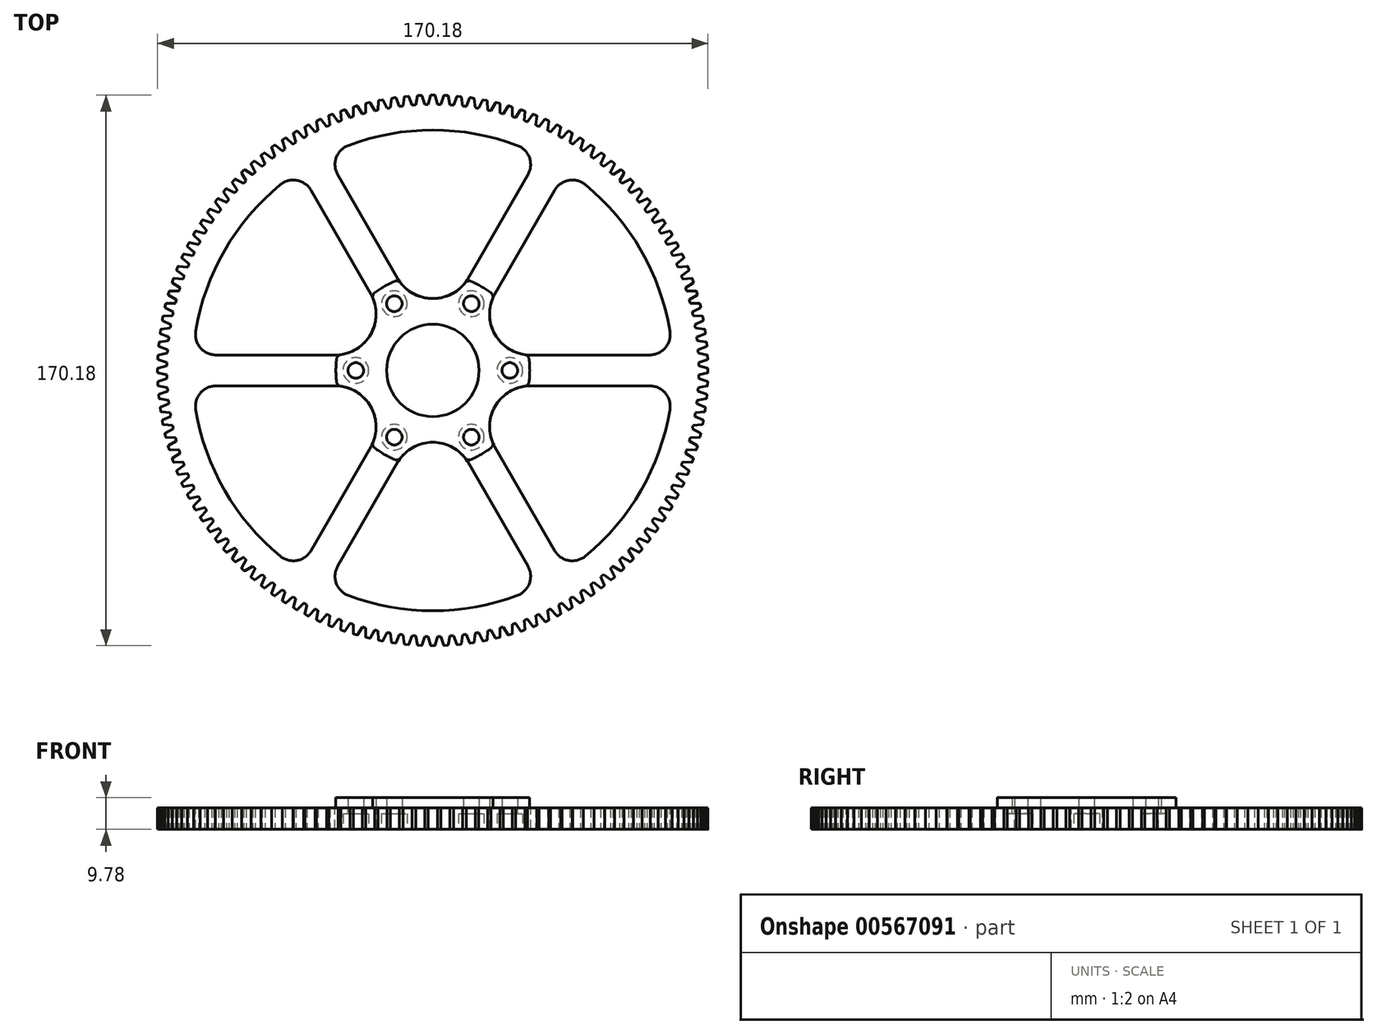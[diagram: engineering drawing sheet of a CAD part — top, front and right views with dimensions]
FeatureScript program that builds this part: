
annotation { "Feature Type Name" : "Feature", "Feature Type Description" : "" }
export const myFeature = defineFeature(function(context is Context, id is Id, definition is map)
    precondition{}
    {
        {
            var Q0;
            Q0=qCreatedBy(makeId("Top.planeOp"),FACE);
            var sketch = newSketch(context, id + "F0", { "sketchPlane" : qUnion([Q0])});
            skArc(sketch, "E0", {"start": v(-1.4, 82.23) * mm, "mid": v(-82.23, -1.4) * mm, "end": v(1.4, -82.23) * mm});
            skArc(sketch, "E1", {"start": v(1.4, -82.23) * mm, "mid": v(82.24, 0) * mm, "end": v(1.4, 82.23) * mm});
            skLineSegment(sketch, "E2", {"start": v(1.4, 82.23) * mm, "end": v(0.7, 84.97) * mm});
            skArc(sketch, "E3", {"start": v(0.7, 84.97) * mm, "mid": v(0.64, 85.06) * mm, "end": v(0.55, 85.1) * mm});
            skLineSegment(sketch, "E4", {"start": v(-1.4, 82.23) * mm, "end": v(-0.7, 84.97) * mm});
            skArc(sketch, "E5", {"start": v(-0.55, 85.1) * mm, "mid": v(-0.64, 85.06) * mm, "end": v(-0.7, 84.97) * mm});
            skLineSegment(sketch, "E6", {"start": v(-0.55, 85.1) * mm, "end": v(0.55, 85.1) * mm});
            skArc(sketch, "E7", {"start": v(1.4, 82.23) * mm, "mid": v(0, 82.24) * mm, "end": v(-1.4, 82.23) * mm});
            skSolve(sketch);
        }
        {
            var Q0;
            Q0=makeQuery(id+"F0.imprint","IMPRINT",FACE,{"disambiguationData":[TD([[makeQuery(id+"F0.imprint","IMPRINT",EDGE,{"derivedFrom":sQuery(id+"F0.wireOp",EDGE,"E0")}),1.0]])]});
            extrude(context, id + "F1", {"entities" : qUnion([Q0]), "endBound" : BoundingType.SYMMETRIC, "depth" : 6.6 * mm, "offsetDistance" : 25.4 * mm});
        }
        {
            var Q0;
            Q0=makeQuery(id+"F0.imprint","IMPRINT",FACE,{"disambiguationData":[TD([[makeQuery(id+"F0.imprint","IMPRINT",EDGE,{"derivedFrom":sQuery(id+"F0.wireOp",EDGE,"E2")}),1.0]])]});
            var Q1;
            Q1=makeQuery(id+"F1.opExtrude","CAP_FACE",FACE,{"disambiguationData":[OSD([sQuery(id+"F0.wireOp",EDGE,"E0"),sQuery(id+"F0.wireOp",EDGE,"E1"),sQuery(id+"F0.wireOp",EDGE,"E7")])],"isStart":false});
            var Q2;
            Q2=makeQuery(id+"F1.opExtrude","CAP_FACE",FACE,{"disambiguationData":[OSD([sQuery(id+"F0.wireOp",EDGE,"E0"),sQuery(id+"F0.wireOp",EDGE,"E1"),sQuery(id+"F0.wireOp",EDGE,"E7")])],"isStart":true});
            extrude(context, id + "F2", {"entities" : qUnion([Q0]), "endBound" : BoundingType.UP_TO_SURFACE, "endBoundEntityFace" : qUnion([Q1]), "depth" : 25.4 * mm, "hasSecondDirection" : true, "secondDirectionBound" : SecondDirectionBoundingType.UP_TO_SURFACE, "secondDirectionOppositeDirection" : true, "secondDirectionBoundEntityFace" : qUnion([Q2]), "secondDirectionDepth" : 25.4 * mm});
        }
        {
            var Q0;
            Q0=makeQuery(id+"F2.opExtrude","SWEPT_BODY",BODY,{"disambiguationData":[OSD([sQuery(id+"F0.wireOp",EDGE,"E2"),sQuery(id+"F0.wireOp",EDGE,"E3"),sQuery(id+"F0.wireOp",EDGE,"E4"),sQuery(id+"F0.wireOp",EDGE,"E5"),sQuery(id+"F0.wireOp",EDGE,"E6"),sQuery(id+"F0.wireOp",EDGE,"E7")])]});
            var Q1;
            Q1=makeQuery(id+"F1.opExtrude","CAP_EDGE",EDGE,{"disambiguationData":[OSD([sQuery(id+"F0.wireOp",EDGE,"E0"),sQuery(id+"F0.wireOp",EDGE,"E1"),sQuery(id+"F0.wireOp",EDGE,"E7")])],"isStart":false});
            circularPattern(context, id + "F3", {"operationType" : NewBodyOperationType.ADD, "entities" : qUnion([Q0]), "axis" : qUnion([Q1]), "angle" : 360 * degree, "instanceCount" : 132, "oppositeDirection" : true, "equalSpace" : true});
        }
        {
            var Q0;
            {var subQ0=sQuery(id+"F0.wireOp",EDGE,"E7");var subQ1=makeQuery(id+"F2.opExtrude","CAP_FACE",FACE,{"disambiguationData":[OSD([sQuery(id+"F0.wireOp",EDGE,"E2"),sQuery(id+"F0.wireOp",EDGE,"E3"),sQuery(id+"F0.wireOp",EDGE,"E4"),sQuery(id+"F0.wireOp",EDGE,"E5"),sQuery(id+"F0.wireOp",EDGE,"E6"),subQ0])],"isStart":false});Q0=makeQuery(id+"F3.boolean.opBoolean","MERGE",FACE,{"derivedFrom":[makeQuery(id+"F1.opExtrude","CAP_FACE",FACE,{"disambiguationData":[OSD([sQuery(id+"F0.wireOp",EDGE,"E0"),sQuery(id+"F0.wireOp",EDGE,"E1"),subQ0])],"isStart":false}),subQ1,makeQuery(id+"F3.opPattern","COPY",FACE,{"derivedFrom":subQ1,"instanceName":"1"}),makeQuery(id+"F3.opPattern","COPY",FACE,{"derivedFrom":subQ1,"instanceName":"2"}),makeQuery(id+"F3.opPattern","COPY",FACE,{"derivedFrom":subQ1,"instanceName":"3"}),makeQuery(id+"F3.opPattern","COPY",FACE,{"derivedFrom":subQ1,"instanceName":"4"}),makeQuery(id+"F3.opPattern","COPY",FACE,{"derivedFrom":subQ1,"instanceName":"5"}),makeQuery(id+"F3.opPattern","COPY",FACE,{"derivedFrom":subQ1,"instanceName":"6"}),makeQuery(id+"F3.opPattern","COPY",FACE,{"derivedFrom":subQ1,"instanceName":"7"}),makeQuery(id+"F3.opPattern","COPY",FACE,{"derivedFrom":subQ1,"instanceName":"8"}),makeQuery(id+"F3.opPattern","COPY",FACE,{"derivedFrom":subQ1,"instanceName":"9"}),makeQuery(id+"F3.opPattern","COPY",FACE,{"derivedFrom":subQ1,"instanceName":"10"}),makeQuery(id+"F3.opPattern","COPY",FACE,{"derivedFrom":subQ1,"instanceName":"11"}),makeQuery(id+"F3.opPattern","COPY",FACE,{"derivedFrom":subQ1,"instanceName":"12"}),makeQuery(id+"F3.opPattern","COPY",FACE,{"derivedFrom":subQ1,"instanceName":"13"}),makeQuery(id+"F3.opPattern","COPY",FACE,{"derivedFrom":subQ1,"instanceName":"14"}),makeQuery(id+"F3.opPattern","COPY",FACE,{"derivedFrom":subQ1,"instanceName":"15"}),makeQuery(id+"F3.opPattern","COPY",FACE,{"derivedFrom":subQ1,"instanceName":"16"}),makeQuery(id+"F3.opPattern","COPY",FACE,{"derivedFrom":subQ1,"instanceName":"17"}),makeQuery(id+"F3.opPattern","COPY",FACE,{"derivedFrom":subQ1,"instanceName":"18"}),makeQuery(id+"F3.opPattern","COPY",FACE,{"derivedFrom":subQ1,"instanceName":"19"}),makeQuery(id+"F3.opPattern","COPY",FACE,{"derivedFrom":subQ1,"instanceName":"20"}),makeQuery(id+"F3.opPattern","COPY",FACE,{"derivedFrom":subQ1,"instanceName":"21"}),makeQuery(id+"F3.opPattern","COPY",FACE,{"derivedFrom":subQ1,"instanceName":"22"}),makeQuery(id+"F3.opPattern","COPY",FACE,{"derivedFrom":subQ1,"instanceName":"23"}),makeQuery(id+"F3.opPattern","COPY",FACE,{"derivedFrom":subQ1,"instanceName":"24"}),makeQuery(id+"F3.opPattern","COPY",FACE,{"derivedFrom":subQ1,"instanceName":"25"}),makeQuery(id+"F3.opPattern","COPY",FACE,{"derivedFrom":subQ1,"instanceName":"26"}),makeQuery(id+"F3.opPattern","COPY",FACE,{"derivedFrom":subQ1,"instanceName":"27"}),makeQuery(id+"F3.opPattern","COPY",FACE,{"derivedFrom":subQ1,"instanceName":"28"}),makeQuery(id+"F3.opPattern","COPY",FACE,{"derivedFrom":subQ1,"instanceName":"29"}),makeQuery(id+"F3.opPattern","COPY",FACE,{"derivedFrom":subQ1,"instanceName":"30"}),makeQuery(id+"F3.opPattern","COPY",FACE,{"derivedFrom":subQ1,"instanceName":"31"}),makeQuery(id+"F3.opPattern","COPY",FACE,{"derivedFrom":subQ1,"instanceName":"32"}),makeQuery(id+"F3.opPattern","COPY",FACE,{"derivedFrom":subQ1,"instanceName":"33"}),makeQuery(id+"F3.opPattern","COPY",FACE,{"derivedFrom":subQ1,"instanceName":"34"}),makeQuery(id+"F3.opPattern","COPY",FACE,{"derivedFrom":subQ1,"instanceName":"35"}),makeQuery(id+"F3.opPattern","COPY",FACE,{"derivedFrom":subQ1,"instanceName":"36"}),makeQuery(id+"F3.opPattern","COPY",FACE,{"derivedFrom":subQ1,"instanceName":"37"}),makeQuery(id+"F3.opPattern","COPY",FACE,{"derivedFrom":subQ1,"instanceName":"38"}),makeQuery(id+"F3.opPattern","COPY",FACE,{"derivedFrom":subQ1,"instanceName":"39"}),makeQuery(id+"F3.opPattern","COPY",FACE,{"derivedFrom":subQ1,"instanceName":"40"}),makeQuery(id+"F3.opPattern","COPY",FACE,{"derivedFrom":subQ1,"instanceName":"41"}),makeQuery(id+"F3.opPattern","COPY",FACE,{"derivedFrom":subQ1,"instanceName":"42"}),makeQuery(id+"F3.opPattern","COPY",FACE,{"derivedFrom":subQ1,"instanceName":"43"}),makeQuery(id+"F3.opPattern","COPY",FACE,{"derivedFrom":subQ1,"instanceName":"44"}),makeQuery(id+"F3.opPattern","COPY",FACE,{"derivedFrom":subQ1,"instanceName":"45"}),makeQuery(id+"F3.opPattern","COPY",FACE,{"derivedFrom":subQ1,"instanceName":"46"}),makeQuery(id+"F3.opPattern","COPY",FACE,{"derivedFrom":subQ1,"instanceName":"47"}),makeQuery(id+"F3.opPattern","COPY",FACE,{"derivedFrom":subQ1,"instanceName":"48"}),makeQuery(id+"F3.opPattern","COPY",FACE,{"derivedFrom":subQ1,"instanceName":"49"}),makeQuery(id+"F3.opPattern","COPY",FACE,{"derivedFrom":subQ1,"instanceName":"50"}),makeQuery(id+"F3.opPattern","COPY",FACE,{"derivedFrom":subQ1,"instanceName":"51"}),makeQuery(id+"F3.opPattern","COPY",FACE,{"derivedFrom":subQ1,"instanceName":"52"}),makeQuery(id+"F3.opPattern","COPY",FACE,{"derivedFrom":subQ1,"instanceName":"53"}),makeQuery(id+"F3.opPattern","COPY",FACE,{"derivedFrom":subQ1,"instanceName":"54"}),makeQuery(id+"F3.opPattern","COPY",FACE,{"derivedFrom":subQ1,"instanceName":"55"}),makeQuery(id+"F3.opPattern","COPY",FACE,{"derivedFrom":subQ1,"instanceName":"56"}),makeQuery(id+"F3.opPattern","COPY",FACE,{"derivedFrom":subQ1,"instanceName":"57"}),makeQuery(id+"F3.opPattern","COPY",FACE,{"derivedFrom":subQ1,"instanceName":"58"}),makeQuery(id+"F3.opPattern","COPY",FACE,{"derivedFrom":subQ1,"instanceName":"59"}),makeQuery(id+"F3.opPattern","COPY",FACE,{"derivedFrom":subQ1,"instanceName":"60"}),makeQuery(id+"F3.opPattern","COPY",FACE,{"derivedFrom":subQ1,"instanceName":"61"}),makeQuery(id+"F3.opPattern","COPY",FACE,{"derivedFrom":subQ1,"instanceName":"62"}),makeQuery(id+"F3.opPattern","COPY",FACE,{"derivedFrom":subQ1,"instanceName":"63"}),makeQuery(id+"F3.opPattern","COPY",FACE,{"derivedFrom":subQ1,"instanceName":"64"}),makeQuery(id+"F3.opPattern","COPY",FACE,{"derivedFrom":subQ1,"instanceName":"65"}),makeQuery(id+"F3.opPattern","COPY",FACE,{"derivedFrom":subQ1,"instanceName":"66"}),makeQuery(id+"F3.opPattern","COPY",FACE,{"derivedFrom":subQ1,"instanceName":"67"}),makeQuery(id+"F3.opPattern","COPY",FACE,{"derivedFrom":subQ1,"instanceName":"68"}),makeQuery(id+"F3.opPattern","COPY",FACE,{"derivedFrom":subQ1,"instanceName":"69"}),makeQuery(id+"F3.opPattern","COPY",FACE,{"derivedFrom":subQ1,"instanceName":"70"}),makeQuery(id+"F3.opPattern","COPY",FACE,{"derivedFrom":subQ1,"instanceName":"71"}),makeQuery(id+"F3.opPattern","COPY",FACE,{"derivedFrom":subQ1,"instanceName":"72"}),makeQuery(id+"F3.opPattern","COPY",FACE,{"derivedFrom":subQ1,"instanceName":"73"}),makeQuery(id+"F3.opPattern","COPY",FACE,{"derivedFrom":subQ1,"instanceName":"74"}),makeQuery(id+"F3.opPattern","COPY",FACE,{"derivedFrom":subQ1,"instanceName":"75"}),makeQuery(id+"F3.opPattern","COPY",FACE,{"derivedFrom":subQ1,"instanceName":"76"}),makeQuery(id+"F3.opPattern","COPY",FACE,{"derivedFrom":subQ1,"instanceName":"77"}),makeQuery(id+"F3.opPattern","COPY",FACE,{"derivedFrom":subQ1,"instanceName":"78"}),makeQuery(id+"F3.opPattern","COPY",FACE,{"derivedFrom":subQ1,"instanceName":"79"}),makeQuery(id+"F3.opPattern","COPY",FACE,{"derivedFrom":subQ1,"instanceName":"80"}),makeQuery(id+"F3.opPattern","COPY",FACE,{"derivedFrom":subQ1,"instanceName":"81"}),makeQuery(id+"F3.opPattern","COPY",FACE,{"derivedFrom":subQ1,"instanceName":"82"}),makeQuery(id+"F3.opPattern","COPY",FACE,{"derivedFrom":subQ1,"instanceName":"83"}),makeQuery(id+"F3.opPattern","COPY",FACE,{"derivedFrom":subQ1,"instanceName":"84"}),makeQuery(id+"F3.opPattern","COPY",FACE,{"derivedFrom":subQ1,"instanceName":"85"}),makeQuery(id+"F3.opPattern","COPY",FACE,{"derivedFrom":subQ1,"instanceName":"86"}),makeQuery(id+"F3.opPattern","COPY",FACE,{"derivedFrom":subQ1,"instanceName":"87"}),makeQuery(id+"F3.opPattern","COPY",FACE,{"derivedFrom":subQ1,"instanceName":"88"}),makeQuery(id+"F3.opPattern","COPY",FACE,{"derivedFrom":subQ1,"instanceName":"89"}),makeQuery(id+"F3.opPattern","COPY",FACE,{"derivedFrom":subQ1,"instanceName":"90"}),makeQuery(id+"F3.opPattern","COPY",FACE,{"derivedFrom":subQ1,"instanceName":"91"}),makeQuery(id+"F3.opPattern","COPY",FACE,{"derivedFrom":subQ1,"instanceName":"92"}),makeQuery(id+"F3.opPattern","COPY",FACE,{"derivedFrom":subQ1,"instanceName":"93"}),makeQuery(id+"F3.opPattern","COPY",FACE,{"derivedFrom":subQ1,"instanceName":"94"}),makeQuery(id+"F3.opPattern","COPY",FACE,{"derivedFrom":subQ1,"instanceName":"95"}),makeQuery(id+"F3.opPattern","COPY",FACE,{"derivedFrom":subQ1,"instanceName":"96"}),makeQuery(id+"F3.opPattern","COPY",FACE,{"derivedFrom":subQ1,"instanceName":"97"}),makeQuery(id+"F3.opPattern","COPY",FACE,{"derivedFrom":subQ1,"instanceName":"98"}),makeQuery(id+"F3.opPattern","COPY",FACE,{"derivedFrom":subQ1,"instanceName":"99"}),makeQuery(id+"F3.opPattern","COPY",FACE,{"derivedFrom":subQ1,"instanceName":"100"}),makeQuery(id+"F3.opPattern","COPY",FACE,{"derivedFrom":subQ1,"instanceName":"101"}),makeQuery(id+"F3.opPattern","COPY",FACE,{"derivedFrom":subQ1,"instanceName":"102"}),makeQuery(id+"F3.opPattern","COPY",FACE,{"derivedFrom":subQ1,"instanceName":"103"}),makeQuery(id+"F3.opPattern","COPY",FACE,{"derivedFrom":subQ1,"instanceName":"104"}),makeQuery(id+"F3.opPattern","COPY",FACE,{"derivedFrom":subQ1,"instanceName":"105"}),makeQuery(id+"F3.opPattern","COPY",FACE,{"derivedFrom":subQ1,"instanceName":"106"}),makeQuery(id+"F3.opPattern","COPY",FACE,{"derivedFrom":subQ1,"instanceName":"107"}),makeQuery(id+"F3.opPattern","COPY",FACE,{"derivedFrom":subQ1,"instanceName":"108"}),makeQuery(id+"F3.opPattern","COPY",FACE,{"derivedFrom":subQ1,"instanceName":"109"}),makeQuery(id+"F3.opPattern","COPY",FACE,{"derivedFrom":subQ1,"instanceName":"110"}),makeQuery(id+"F3.opPattern","COPY",FACE,{"derivedFrom":subQ1,"instanceName":"111"}),makeQuery(id+"F3.opPattern","COPY",FACE,{"derivedFrom":subQ1,"instanceName":"112"}),makeQuery(id+"F3.opPattern","COPY",FACE,{"derivedFrom":subQ1,"instanceName":"113"}),makeQuery(id+"F3.opPattern","COPY",FACE,{"derivedFrom":subQ1,"instanceName":"114"}),makeQuery(id+"F3.opPattern","COPY",FACE,{"derivedFrom":subQ1,"instanceName":"115"}),makeQuery(id+"F3.opPattern","COPY",FACE,{"derivedFrom":subQ1,"instanceName":"116"}),makeQuery(id+"F3.opPattern","COPY",FACE,{"derivedFrom":subQ1,"instanceName":"117"}),makeQuery(id+"F3.opPattern","COPY",FACE,{"derivedFrom":subQ1,"instanceName":"118"}),makeQuery(id+"F3.opPattern","COPY",FACE,{"derivedFrom":subQ1,"instanceName":"119"}),makeQuery(id+"F3.opPattern","COPY",FACE,{"derivedFrom":subQ1,"instanceName":"120"}),makeQuery(id+"F3.opPattern","COPY",FACE,{"derivedFrom":subQ1,"instanceName":"121"}),makeQuery(id+"F3.opPattern","COPY",FACE,{"derivedFrom":subQ1,"instanceName":"122"}),makeQuery(id+"F3.opPattern","COPY",FACE,{"derivedFrom":subQ1,"instanceName":"123"}),makeQuery(id+"F3.opPattern","COPY",FACE,{"derivedFrom":subQ1,"instanceName":"124"}),makeQuery(id+"F3.opPattern","COPY",FACE,{"derivedFrom":subQ1,"instanceName":"125"}),makeQuery(id+"F3.opPattern","COPY",FACE,{"derivedFrom":subQ1,"instanceName":"126"}),makeQuery(id+"F3.opPattern","COPY",FACE,{"derivedFrom":subQ1,"instanceName":"127"}),makeQuery(id+"F3.opPattern","COPY",FACE,{"derivedFrom":subQ1,"instanceName":"128"}),makeQuery(id+"F3.opPattern","COPY",FACE,{"derivedFrom":subQ1,"instanceName":"129"}),makeQuery(id+"F3.opPattern","COPY",FACE,{"derivedFrom":subQ1,"instanceName":"130"}),makeQuery(id+"F3.opPattern","COPY",FACE,{"derivedFrom":subQ1,"instanceName":"131"})]});}
            var sketch = newSketch(context, id + "F4", { "sketchPlane" : qUnion([Q0])});
            skCircle(sketch, "E8", {"center": v(0, 0) * mm, "radius": 14.29 * mm});
            skCircle(sketch, "E9.cCircle", {"center": v(0, 0) * mm, "radius": 23.81 * mm, "construction": true});
            skLineSegment(sketch, "E9.0", {"start": v(23.81, 0) * mm, "end": v(11.9, -20.62) * mm, "construction": true});
            skLineSegment(sketch, "E9.1", {"start": v(11.9, -20.62) * mm, "end": v(-11.9, -20.62) * mm, "construction": true});
            skLineSegment(sketch, "E9.2", {"start": v(-11.9, -20.62) * mm, "end": v(-23.81, 0) * mm, "construction": true});
            skLineSegment(sketch, "E9.3", {"start": v(-23.81, 0) * mm, "end": v(-11.9, 20.62) * mm, "construction": true});
            skLineSegment(sketch, "E9.4", {"start": v(-11.9, 20.62) * mm, "end": v(11.9, 20.62) * mm, "construction": true});
            skLineSegment(sketch, "E9.5", {"start": v(11.9, 20.62) * mm, "end": v(23.81, 0) * mm, "construction": true});
            skCircle(sketch, "E10", {"center": v(-11.9, 20.62) * mm, "radius": 2.41 * mm});
            skCircle(sketch, "E11", {"center": v(-23.81, 0) * mm, "radius": 2.41 * mm});
            skCircle(sketch, "E12", {"center": v(-11.9, -20.62) * mm, "radius": 2.41 * mm});
            skCircle(sketch, "E13", {"center": v(11.9, -20.62) * mm, "radius": 2.41 * mm});
            skCircle(sketch, "E14", {"center": v(23.81, 0) * mm, "radius": 2.41 * mm});
            skCircle(sketch, "E15", {"center": v(11.9, 20.62) * mm, "radius": 2.41 * mm});
            skSolve(sketch);
        }
        {
            var Q0;
            Q0=qSketchRegion(id+"F4",true);
            extrude(context, id + "F5", {"entities" : qUnion([Q0]), "operationType" : NewBodyOperationType.REMOVE, "endBound" : BoundingType.THROUGH_ALL, "oppositeDirection" : true, "depth" : 25.4 * mm});
        }
        {
            var Q0;
            {var subQ0=sQuery(id+"F0.wireOp",EDGE,"E7");var subQ1=makeQuery(id+"F2.opExtrude","CAP_FACE",FACE,{"disambiguationData":[OSD([sQuery(id+"F0.wireOp",EDGE,"E2"),sQuery(id+"F0.wireOp",EDGE,"E3"),sQuery(id+"F0.wireOp",EDGE,"E4"),sQuery(id+"F0.wireOp",EDGE,"E5"),sQuery(id+"F0.wireOp",EDGE,"E6"),subQ0])],"isStart":false});Q0=makeQuery(id+"F3.boolean.opBoolean","MERGE",FACE,{"derivedFrom":[makeQuery(id+"F1.opExtrude","CAP_FACE",FACE,{"disambiguationData":[OSD([sQuery(id+"F0.wireOp",EDGE,"E0"),sQuery(id+"F0.wireOp",EDGE,"E1"),subQ0])],"isStart":false}),subQ1,makeQuery(id+"F3.opPattern","COPY",FACE,{"derivedFrom":subQ1,"instanceName":"1"}),makeQuery(id+"F3.opPattern","COPY",FACE,{"derivedFrom":subQ1,"instanceName":"2"}),makeQuery(id+"F3.opPattern","COPY",FACE,{"derivedFrom":subQ1,"instanceName":"3"}),makeQuery(id+"F3.opPattern","COPY",FACE,{"derivedFrom":subQ1,"instanceName":"4"}),makeQuery(id+"F3.opPattern","COPY",FACE,{"derivedFrom":subQ1,"instanceName":"5"}),makeQuery(id+"F3.opPattern","COPY",FACE,{"derivedFrom":subQ1,"instanceName":"6"}),makeQuery(id+"F3.opPattern","COPY",FACE,{"derivedFrom":subQ1,"instanceName":"7"}),makeQuery(id+"F3.opPattern","COPY",FACE,{"derivedFrom":subQ1,"instanceName":"8"}),makeQuery(id+"F3.opPattern","COPY",FACE,{"derivedFrom":subQ1,"instanceName":"9"}),makeQuery(id+"F3.opPattern","COPY",FACE,{"derivedFrom":subQ1,"instanceName":"10"}),makeQuery(id+"F3.opPattern","COPY",FACE,{"derivedFrom":subQ1,"instanceName":"11"}),makeQuery(id+"F3.opPattern","COPY",FACE,{"derivedFrom":subQ1,"instanceName":"12"}),makeQuery(id+"F3.opPattern","COPY",FACE,{"derivedFrom":subQ1,"instanceName":"13"}),makeQuery(id+"F3.opPattern","COPY",FACE,{"derivedFrom":subQ1,"instanceName":"14"}),makeQuery(id+"F3.opPattern","COPY",FACE,{"derivedFrom":subQ1,"instanceName":"15"}),makeQuery(id+"F3.opPattern","COPY",FACE,{"derivedFrom":subQ1,"instanceName":"16"}),makeQuery(id+"F3.opPattern","COPY",FACE,{"derivedFrom":subQ1,"instanceName":"17"}),makeQuery(id+"F3.opPattern","COPY",FACE,{"derivedFrom":subQ1,"instanceName":"18"}),makeQuery(id+"F3.opPattern","COPY",FACE,{"derivedFrom":subQ1,"instanceName":"19"}),makeQuery(id+"F3.opPattern","COPY",FACE,{"derivedFrom":subQ1,"instanceName":"20"}),makeQuery(id+"F3.opPattern","COPY",FACE,{"derivedFrom":subQ1,"instanceName":"21"}),makeQuery(id+"F3.opPattern","COPY",FACE,{"derivedFrom":subQ1,"instanceName":"22"}),makeQuery(id+"F3.opPattern","COPY",FACE,{"derivedFrom":subQ1,"instanceName":"23"}),makeQuery(id+"F3.opPattern","COPY",FACE,{"derivedFrom":subQ1,"instanceName":"24"}),makeQuery(id+"F3.opPattern","COPY",FACE,{"derivedFrom":subQ1,"instanceName":"25"}),makeQuery(id+"F3.opPattern","COPY",FACE,{"derivedFrom":subQ1,"instanceName":"26"}),makeQuery(id+"F3.opPattern","COPY",FACE,{"derivedFrom":subQ1,"instanceName":"27"}),makeQuery(id+"F3.opPattern","COPY",FACE,{"derivedFrom":subQ1,"instanceName":"28"}),makeQuery(id+"F3.opPattern","COPY",FACE,{"derivedFrom":subQ1,"instanceName":"29"}),makeQuery(id+"F3.opPattern","COPY",FACE,{"derivedFrom":subQ1,"instanceName":"30"}),makeQuery(id+"F3.opPattern","COPY",FACE,{"derivedFrom":subQ1,"instanceName":"31"}),makeQuery(id+"F3.opPattern","COPY",FACE,{"derivedFrom":subQ1,"instanceName":"32"}),makeQuery(id+"F3.opPattern","COPY",FACE,{"derivedFrom":subQ1,"instanceName":"33"}),makeQuery(id+"F3.opPattern","COPY",FACE,{"derivedFrom":subQ1,"instanceName":"34"}),makeQuery(id+"F3.opPattern","COPY",FACE,{"derivedFrom":subQ1,"instanceName":"35"}),makeQuery(id+"F3.opPattern","COPY",FACE,{"derivedFrom":subQ1,"instanceName":"36"}),makeQuery(id+"F3.opPattern","COPY",FACE,{"derivedFrom":subQ1,"instanceName":"37"}),makeQuery(id+"F3.opPattern","COPY",FACE,{"derivedFrom":subQ1,"instanceName":"38"}),makeQuery(id+"F3.opPattern","COPY",FACE,{"derivedFrom":subQ1,"instanceName":"39"}),makeQuery(id+"F3.opPattern","COPY",FACE,{"derivedFrom":subQ1,"instanceName":"40"}),makeQuery(id+"F3.opPattern","COPY",FACE,{"derivedFrom":subQ1,"instanceName":"41"}),makeQuery(id+"F3.opPattern","COPY",FACE,{"derivedFrom":subQ1,"instanceName":"42"}),makeQuery(id+"F3.opPattern","COPY",FACE,{"derivedFrom":subQ1,"instanceName":"43"}),makeQuery(id+"F3.opPattern","COPY",FACE,{"derivedFrom":subQ1,"instanceName":"44"}),makeQuery(id+"F3.opPattern","COPY",FACE,{"derivedFrom":subQ1,"instanceName":"45"}),makeQuery(id+"F3.opPattern","COPY",FACE,{"derivedFrom":subQ1,"instanceName":"46"}),makeQuery(id+"F3.opPattern","COPY",FACE,{"derivedFrom":subQ1,"instanceName":"47"}),makeQuery(id+"F3.opPattern","COPY",FACE,{"derivedFrom":subQ1,"instanceName":"48"}),makeQuery(id+"F3.opPattern","COPY",FACE,{"derivedFrom":subQ1,"instanceName":"49"}),makeQuery(id+"F3.opPattern","COPY",FACE,{"derivedFrom":subQ1,"instanceName":"50"}),makeQuery(id+"F3.opPattern","COPY",FACE,{"derivedFrom":subQ1,"instanceName":"51"}),makeQuery(id+"F3.opPattern","COPY",FACE,{"derivedFrom":subQ1,"instanceName":"52"}),makeQuery(id+"F3.opPattern","COPY",FACE,{"derivedFrom":subQ1,"instanceName":"53"}),makeQuery(id+"F3.opPattern","COPY",FACE,{"derivedFrom":subQ1,"instanceName":"54"}),makeQuery(id+"F3.opPattern","COPY",FACE,{"derivedFrom":subQ1,"instanceName":"55"}),makeQuery(id+"F3.opPattern","COPY",FACE,{"derivedFrom":subQ1,"instanceName":"56"}),makeQuery(id+"F3.opPattern","COPY",FACE,{"derivedFrom":subQ1,"instanceName":"57"}),makeQuery(id+"F3.opPattern","COPY",FACE,{"derivedFrom":subQ1,"instanceName":"58"}),makeQuery(id+"F3.opPattern","COPY",FACE,{"derivedFrom":subQ1,"instanceName":"59"}),makeQuery(id+"F3.opPattern","COPY",FACE,{"derivedFrom":subQ1,"instanceName":"60"}),makeQuery(id+"F3.opPattern","COPY",FACE,{"derivedFrom":subQ1,"instanceName":"61"}),makeQuery(id+"F3.opPattern","COPY",FACE,{"derivedFrom":subQ1,"instanceName":"62"}),makeQuery(id+"F3.opPattern","COPY",FACE,{"derivedFrom":subQ1,"instanceName":"63"}),makeQuery(id+"F3.opPattern","COPY",FACE,{"derivedFrom":subQ1,"instanceName":"64"}),makeQuery(id+"F3.opPattern","COPY",FACE,{"derivedFrom":subQ1,"instanceName":"65"}),makeQuery(id+"F3.opPattern","COPY",FACE,{"derivedFrom":subQ1,"instanceName":"66"}),makeQuery(id+"F3.opPattern","COPY",FACE,{"derivedFrom":subQ1,"instanceName":"67"}),makeQuery(id+"F3.opPattern","COPY",FACE,{"derivedFrom":subQ1,"instanceName":"68"}),makeQuery(id+"F3.opPattern","COPY",FACE,{"derivedFrom":subQ1,"instanceName":"69"}),makeQuery(id+"F3.opPattern","COPY",FACE,{"derivedFrom":subQ1,"instanceName":"70"}),makeQuery(id+"F3.opPattern","COPY",FACE,{"derivedFrom":subQ1,"instanceName":"71"}),makeQuery(id+"F3.opPattern","COPY",FACE,{"derivedFrom":subQ1,"instanceName":"72"}),makeQuery(id+"F3.opPattern","COPY",FACE,{"derivedFrom":subQ1,"instanceName":"73"}),makeQuery(id+"F3.opPattern","COPY",FACE,{"derivedFrom":subQ1,"instanceName":"74"}),makeQuery(id+"F3.opPattern","COPY",FACE,{"derivedFrom":subQ1,"instanceName":"75"}),makeQuery(id+"F3.opPattern","COPY",FACE,{"derivedFrom":subQ1,"instanceName":"76"}),makeQuery(id+"F3.opPattern","COPY",FACE,{"derivedFrom":subQ1,"instanceName":"77"}),makeQuery(id+"F3.opPattern","COPY",FACE,{"derivedFrom":subQ1,"instanceName":"78"}),makeQuery(id+"F3.opPattern","COPY",FACE,{"derivedFrom":subQ1,"instanceName":"79"}),makeQuery(id+"F3.opPattern","COPY",FACE,{"derivedFrom":subQ1,"instanceName":"80"}),makeQuery(id+"F3.opPattern","COPY",FACE,{"derivedFrom":subQ1,"instanceName":"81"}),makeQuery(id+"F3.opPattern","COPY",FACE,{"derivedFrom":subQ1,"instanceName":"82"}),makeQuery(id+"F3.opPattern","COPY",FACE,{"derivedFrom":subQ1,"instanceName":"83"}),makeQuery(id+"F3.opPattern","COPY",FACE,{"derivedFrom":subQ1,"instanceName":"84"}),makeQuery(id+"F3.opPattern","COPY",FACE,{"derivedFrom":subQ1,"instanceName":"85"}),makeQuery(id+"F3.opPattern","COPY",FACE,{"derivedFrom":subQ1,"instanceName":"86"}),makeQuery(id+"F3.opPattern","COPY",FACE,{"derivedFrom":subQ1,"instanceName":"87"}),makeQuery(id+"F3.opPattern","COPY",FACE,{"derivedFrom":subQ1,"instanceName":"88"}),makeQuery(id+"F3.opPattern","COPY",FACE,{"derivedFrom":subQ1,"instanceName":"89"}),makeQuery(id+"F3.opPattern","COPY",FACE,{"derivedFrom":subQ1,"instanceName":"90"}),makeQuery(id+"F3.opPattern","COPY",FACE,{"derivedFrom":subQ1,"instanceName":"91"}),makeQuery(id+"F3.opPattern","COPY",FACE,{"derivedFrom":subQ1,"instanceName":"92"}),makeQuery(id+"F3.opPattern","COPY",FACE,{"derivedFrom":subQ1,"instanceName":"93"}),makeQuery(id+"F3.opPattern","COPY",FACE,{"derivedFrom":subQ1,"instanceName":"94"}),makeQuery(id+"F3.opPattern","COPY",FACE,{"derivedFrom":subQ1,"instanceName":"95"}),makeQuery(id+"F3.opPattern","COPY",FACE,{"derivedFrom":subQ1,"instanceName":"96"}),makeQuery(id+"F3.opPattern","COPY",FACE,{"derivedFrom":subQ1,"instanceName":"97"}),makeQuery(id+"F3.opPattern","COPY",FACE,{"derivedFrom":subQ1,"instanceName":"98"}),makeQuery(id+"F3.opPattern","COPY",FACE,{"derivedFrom":subQ1,"instanceName":"99"}),makeQuery(id+"F3.opPattern","COPY",FACE,{"derivedFrom":subQ1,"instanceName":"100"}),makeQuery(id+"F3.opPattern","COPY",FACE,{"derivedFrom":subQ1,"instanceName":"101"}),makeQuery(id+"F3.opPattern","COPY",FACE,{"derivedFrom":subQ1,"instanceName":"102"}),makeQuery(id+"F3.opPattern","COPY",FACE,{"derivedFrom":subQ1,"instanceName":"103"}),makeQuery(id+"F3.opPattern","COPY",FACE,{"derivedFrom":subQ1,"instanceName":"104"}),makeQuery(id+"F3.opPattern","COPY",FACE,{"derivedFrom":subQ1,"instanceName":"105"}),makeQuery(id+"F3.opPattern","COPY",FACE,{"derivedFrom":subQ1,"instanceName":"106"}),makeQuery(id+"F3.opPattern","COPY",FACE,{"derivedFrom":subQ1,"instanceName":"107"}),makeQuery(id+"F3.opPattern","COPY",FACE,{"derivedFrom":subQ1,"instanceName":"108"}),makeQuery(id+"F3.opPattern","COPY",FACE,{"derivedFrom":subQ1,"instanceName":"109"}),makeQuery(id+"F3.opPattern","COPY",FACE,{"derivedFrom":subQ1,"instanceName":"110"}),makeQuery(id+"F3.opPattern","COPY",FACE,{"derivedFrom":subQ1,"instanceName":"111"}),makeQuery(id+"F3.opPattern","COPY",FACE,{"derivedFrom":subQ1,"instanceName":"112"}),makeQuery(id+"F3.opPattern","COPY",FACE,{"derivedFrom":subQ1,"instanceName":"113"}),makeQuery(id+"F3.opPattern","COPY",FACE,{"derivedFrom":subQ1,"instanceName":"114"}),makeQuery(id+"F3.opPattern","COPY",FACE,{"derivedFrom":subQ1,"instanceName":"115"}),makeQuery(id+"F3.opPattern","COPY",FACE,{"derivedFrom":subQ1,"instanceName":"116"}),makeQuery(id+"F3.opPattern","COPY",FACE,{"derivedFrom":subQ1,"instanceName":"117"}),makeQuery(id+"F3.opPattern","COPY",FACE,{"derivedFrom":subQ1,"instanceName":"118"}),makeQuery(id+"F3.opPattern","COPY",FACE,{"derivedFrom":subQ1,"instanceName":"119"}),makeQuery(id+"F3.opPattern","COPY",FACE,{"derivedFrom":subQ1,"instanceName":"120"}),makeQuery(id+"F3.opPattern","COPY",FACE,{"derivedFrom":subQ1,"instanceName":"121"}),makeQuery(id+"F3.opPattern","COPY",FACE,{"derivedFrom":subQ1,"instanceName":"122"}),makeQuery(id+"F3.opPattern","COPY",FACE,{"derivedFrom":subQ1,"instanceName":"123"}),makeQuery(id+"F3.opPattern","COPY",FACE,{"derivedFrom":subQ1,"instanceName":"124"}),makeQuery(id+"F3.opPattern","COPY",FACE,{"derivedFrom":subQ1,"instanceName":"125"}),makeQuery(id+"F3.opPattern","COPY",FACE,{"derivedFrom":subQ1,"instanceName":"126"}),makeQuery(id+"F3.opPattern","COPY",FACE,{"derivedFrom":subQ1,"instanceName":"127"}),makeQuery(id+"F3.opPattern","COPY",FACE,{"derivedFrom":subQ1,"instanceName":"128"}),makeQuery(id+"F3.opPattern","COPY",FACE,{"derivedFrom":subQ1,"instanceName":"129"}),makeQuery(id+"F3.opPattern","COPY",FACE,{"derivedFrom":subQ1,"instanceName":"130"}),makeQuery(id+"F3.opPattern","COPY",FACE,{"derivedFrom":subQ1,"instanceName":"131"})]});}
            var sketch = newSketch(context, id + "F6", { "sketchPlane" : qUnion([Q0])});
            skArc(sketch, "E16", {"start": v(-37.15, 64.35) * mm, "mid": v(-64.35, 37.15) * mm, "end": v(-74.3, 0) * mm});
            skArc(sketch, "E17", {"start": v(-15.08, 26.12) * mm, "mid": v(-26.12, 15.08) * mm, "end": v(-30.16, 0) * mm});
            skLineSegment(sketch, "E18", {"start": v(-15.08, 26.12) * mm, "end": v(-37.15, 64.35) * mm, "construction": true});
            skLineSegment(sketch, "E19", {"start": v(-30.16, 0) * mm, "end": v(-74.3, 0) * mm, "construction": true});
            skPoint(sketch, "E20", {"position": v(-23.81, 0) * mm});
            skLineSegment(sketch, "E21.0", {"start": v(-29.78, 4.77) * mm, "end": v(-74.15, 4.77) * mm});
            skLineSegment(sketch, "E22.0", {"start": v(-19.02, 23.4) * mm, "end": v(-41.2, 61.83) * mm});
            skPoint(sketch, "E23", {"position": v(-11.9, 20.62) * mm});
            skArc(sketch, "E24", {"start": v(-29.78, 4.77) * mm, "mid": v(-19.25, 11.11) * mm, "end": v(-19.02, 23.4) * mm});
            skCircle(sketch, "E25", {"center": v(0, 0) * mm, "radius": 34.93 * mm, "construction": true});
            skLineSegment(sketch, "E26", {"start": v(-26.12, 15.08) * mm, "end": v(0, 0) * mm, "construction": true});
            skSolve(sketch);
        }
        {
            var Q0;
            {var subQ0=sQuery(id+"F6.wireOp",EDGE,"E21.0");Q0=makeQuery(id+"F6.imprint","IMPRINT",FACE,{"disambiguationData":[TD([[makeQuery(id+"F6.imprint","IMPRINT",EDGE,{"derivedFrom":subQ0}),-1.0]])]});}
            var Q1;
            {var subQ0=sQuery(id+"F6.wireOp",EDGE,"E24");Q1=makeQuery(id+"F6.imprint","IMPRINT",FACE,{"disambiguationData":[TD([[makeQuery(id+"F6.imprint","IMPRINT",EDGE,{"derivedFrom":subQ0}),1.0]])]});}
            var Q2;
            {var subQ0=sQuery(id+"F0.wireOp",EDGE,"E7");var subQ1=makeQuery(id+"F2.opExtrude","CAP_FACE",FACE,{"disambiguationData":[OSD([sQuery(id+"F0.wireOp",EDGE,"E2"),sQuery(id+"F0.wireOp",EDGE,"E3"),sQuery(id+"F0.wireOp",EDGE,"E4"),sQuery(id+"F0.wireOp",EDGE,"E5"),sQuery(id+"F0.wireOp",EDGE,"E6"),subQ0])],"isStart":true});Q2=makeQuery(id+"F3.boolean.opBoolean","MERGE",FACE,{"derivedFrom":[makeQuery(id+"F1.opExtrude","CAP_FACE",FACE,{"disambiguationData":[OSD([sQuery(id+"F0.wireOp",EDGE,"E0"),sQuery(id+"F0.wireOp",EDGE,"E1"),subQ0])],"isStart":true}),subQ1,makeQuery(id+"F3.opPattern","COPY",FACE,{"derivedFrom":subQ1,"instanceName":"1"}),makeQuery(id+"F3.opPattern","COPY",FACE,{"derivedFrom":subQ1,"instanceName":"2"}),makeQuery(id+"F3.opPattern","COPY",FACE,{"derivedFrom":subQ1,"instanceName":"3"}),makeQuery(id+"F3.opPattern","COPY",FACE,{"derivedFrom":subQ1,"instanceName":"4"}),makeQuery(id+"F3.opPattern","COPY",FACE,{"derivedFrom":subQ1,"instanceName":"5"}),makeQuery(id+"F3.opPattern","COPY",FACE,{"derivedFrom":subQ1,"instanceName":"6"}),makeQuery(id+"F3.opPattern","COPY",FACE,{"derivedFrom":subQ1,"instanceName":"7"}),makeQuery(id+"F3.opPattern","COPY",FACE,{"derivedFrom":subQ1,"instanceName":"8"}),makeQuery(id+"F3.opPattern","COPY",FACE,{"derivedFrom":subQ1,"instanceName":"9"}),makeQuery(id+"F3.opPattern","COPY",FACE,{"derivedFrom":subQ1,"instanceName":"10"}),makeQuery(id+"F3.opPattern","COPY",FACE,{"derivedFrom":subQ1,"instanceName":"11"}),makeQuery(id+"F3.opPattern","COPY",FACE,{"derivedFrom":subQ1,"instanceName":"12"}),makeQuery(id+"F3.opPattern","COPY",FACE,{"derivedFrom":subQ1,"instanceName":"13"}),makeQuery(id+"F3.opPattern","COPY",FACE,{"derivedFrom":subQ1,"instanceName":"14"}),makeQuery(id+"F3.opPattern","COPY",FACE,{"derivedFrom":subQ1,"instanceName":"15"}),makeQuery(id+"F3.opPattern","COPY",FACE,{"derivedFrom":subQ1,"instanceName":"16"}),makeQuery(id+"F3.opPattern","COPY",FACE,{"derivedFrom":subQ1,"instanceName":"17"}),makeQuery(id+"F3.opPattern","COPY",FACE,{"derivedFrom":subQ1,"instanceName":"18"}),makeQuery(id+"F3.opPattern","COPY",FACE,{"derivedFrom":subQ1,"instanceName":"19"}),makeQuery(id+"F3.opPattern","COPY",FACE,{"derivedFrom":subQ1,"instanceName":"20"}),makeQuery(id+"F3.opPattern","COPY",FACE,{"derivedFrom":subQ1,"instanceName":"21"}),makeQuery(id+"F3.opPattern","COPY",FACE,{"derivedFrom":subQ1,"instanceName":"22"}),makeQuery(id+"F3.opPattern","COPY",FACE,{"derivedFrom":subQ1,"instanceName":"23"}),makeQuery(id+"F3.opPattern","COPY",FACE,{"derivedFrom":subQ1,"instanceName":"24"}),makeQuery(id+"F3.opPattern","COPY",FACE,{"derivedFrom":subQ1,"instanceName":"25"}),makeQuery(id+"F3.opPattern","COPY",FACE,{"derivedFrom":subQ1,"instanceName":"26"}),makeQuery(id+"F3.opPattern","COPY",FACE,{"derivedFrom":subQ1,"instanceName":"27"}),makeQuery(id+"F3.opPattern","COPY",FACE,{"derivedFrom":subQ1,"instanceName":"28"}),makeQuery(id+"F3.opPattern","COPY",FACE,{"derivedFrom":subQ1,"instanceName":"29"}),makeQuery(id+"F3.opPattern","COPY",FACE,{"derivedFrom":subQ1,"instanceName":"30"}),makeQuery(id+"F3.opPattern","COPY",FACE,{"derivedFrom":subQ1,"instanceName":"31"}),makeQuery(id+"F3.opPattern","COPY",FACE,{"derivedFrom":subQ1,"instanceName":"32"}),makeQuery(id+"F3.opPattern","COPY",FACE,{"derivedFrom":subQ1,"instanceName":"33"}),makeQuery(id+"F3.opPattern","COPY",FACE,{"derivedFrom":subQ1,"instanceName":"34"}),makeQuery(id+"F3.opPattern","COPY",FACE,{"derivedFrom":subQ1,"instanceName":"35"}),makeQuery(id+"F3.opPattern","COPY",FACE,{"derivedFrom":subQ1,"instanceName":"36"}),makeQuery(id+"F3.opPattern","COPY",FACE,{"derivedFrom":subQ1,"instanceName":"37"}),makeQuery(id+"F3.opPattern","COPY",FACE,{"derivedFrom":subQ1,"instanceName":"38"}),makeQuery(id+"F3.opPattern","COPY",FACE,{"derivedFrom":subQ1,"instanceName":"39"}),makeQuery(id+"F3.opPattern","COPY",FACE,{"derivedFrom":subQ1,"instanceName":"40"}),makeQuery(id+"F3.opPattern","COPY",FACE,{"derivedFrom":subQ1,"instanceName":"41"}),makeQuery(id+"F3.opPattern","COPY",FACE,{"derivedFrom":subQ1,"instanceName":"42"}),makeQuery(id+"F3.opPattern","COPY",FACE,{"derivedFrom":subQ1,"instanceName":"43"}),makeQuery(id+"F3.opPattern","COPY",FACE,{"derivedFrom":subQ1,"instanceName":"44"}),makeQuery(id+"F3.opPattern","COPY",FACE,{"derivedFrom":subQ1,"instanceName":"45"}),makeQuery(id+"F3.opPattern","COPY",FACE,{"derivedFrom":subQ1,"instanceName":"46"}),makeQuery(id+"F3.opPattern","COPY",FACE,{"derivedFrom":subQ1,"instanceName":"47"}),makeQuery(id+"F3.opPattern","COPY",FACE,{"derivedFrom":subQ1,"instanceName":"48"}),makeQuery(id+"F3.opPattern","COPY",FACE,{"derivedFrom":subQ1,"instanceName":"49"}),makeQuery(id+"F3.opPattern","COPY",FACE,{"derivedFrom":subQ1,"instanceName":"50"}),makeQuery(id+"F3.opPattern","COPY",FACE,{"derivedFrom":subQ1,"instanceName":"51"}),makeQuery(id+"F3.opPattern","COPY",FACE,{"derivedFrom":subQ1,"instanceName":"52"}),makeQuery(id+"F3.opPattern","COPY",FACE,{"derivedFrom":subQ1,"instanceName":"53"}),makeQuery(id+"F3.opPattern","COPY",FACE,{"derivedFrom":subQ1,"instanceName":"54"}),makeQuery(id+"F3.opPattern","COPY",FACE,{"derivedFrom":subQ1,"instanceName":"55"}),makeQuery(id+"F3.opPattern","COPY",FACE,{"derivedFrom":subQ1,"instanceName":"56"}),makeQuery(id+"F3.opPattern","COPY",FACE,{"derivedFrom":subQ1,"instanceName":"57"}),makeQuery(id+"F3.opPattern","COPY",FACE,{"derivedFrom":subQ1,"instanceName":"58"}),makeQuery(id+"F3.opPattern","COPY",FACE,{"derivedFrom":subQ1,"instanceName":"59"}),makeQuery(id+"F3.opPattern","COPY",FACE,{"derivedFrom":subQ1,"instanceName":"60"}),makeQuery(id+"F3.opPattern","COPY",FACE,{"derivedFrom":subQ1,"instanceName":"61"}),makeQuery(id+"F3.opPattern","COPY",FACE,{"derivedFrom":subQ1,"instanceName":"62"}),makeQuery(id+"F3.opPattern","COPY",FACE,{"derivedFrom":subQ1,"instanceName":"63"}),makeQuery(id+"F3.opPattern","COPY",FACE,{"derivedFrom":subQ1,"instanceName":"64"}),makeQuery(id+"F3.opPattern","COPY",FACE,{"derivedFrom":subQ1,"instanceName":"65"}),makeQuery(id+"F3.opPattern","COPY",FACE,{"derivedFrom":subQ1,"instanceName":"66"}),makeQuery(id+"F3.opPattern","COPY",FACE,{"derivedFrom":subQ1,"instanceName":"67"}),makeQuery(id+"F3.opPattern","COPY",FACE,{"derivedFrom":subQ1,"instanceName":"68"}),makeQuery(id+"F3.opPattern","COPY",FACE,{"derivedFrom":subQ1,"instanceName":"69"}),makeQuery(id+"F3.opPattern","COPY",FACE,{"derivedFrom":subQ1,"instanceName":"70"}),makeQuery(id+"F3.opPattern","COPY",FACE,{"derivedFrom":subQ1,"instanceName":"71"}),makeQuery(id+"F3.opPattern","COPY",FACE,{"derivedFrom":subQ1,"instanceName":"72"}),makeQuery(id+"F3.opPattern","COPY",FACE,{"derivedFrom":subQ1,"instanceName":"73"}),makeQuery(id+"F3.opPattern","COPY",FACE,{"derivedFrom":subQ1,"instanceName":"74"}),makeQuery(id+"F3.opPattern","COPY",FACE,{"derivedFrom":subQ1,"instanceName":"75"}),makeQuery(id+"F3.opPattern","COPY",FACE,{"derivedFrom":subQ1,"instanceName":"76"}),makeQuery(id+"F3.opPattern","COPY",FACE,{"derivedFrom":subQ1,"instanceName":"77"}),makeQuery(id+"F3.opPattern","COPY",FACE,{"derivedFrom":subQ1,"instanceName":"78"}),makeQuery(id+"F3.opPattern","COPY",FACE,{"derivedFrom":subQ1,"instanceName":"79"}),makeQuery(id+"F3.opPattern","COPY",FACE,{"derivedFrom":subQ1,"instanceName":"80"}),makeQuery(id+"F3.opPattern","COPY",FACE,{"derivedFrom":subQ1,"instanceName":"81"}),makeQuery(id+"F3.opPattern","COPY",FACE,{"derivedFrom":subQ1,"instanceName":"82"}),makeQuery(id+"F3.opPattern","COPY",FACE,{"derivedFrom":subQ1,"instanceName":"83"}),makeQuery(id+"F3.opPattern","COPY",FACE,{"derivedFrom":subQ1,"instanceName":"84"}),makeQuery(id+"F3.opPattern","COPY",FACE,{"derivedFrom":subQ1,"instanceName":"85"}),makeQuery(id+"F3.opPattern","COPY",FACE,{"derivedFrom":subQ1,"instanceName":"86"}),makeQuery(id+"F3.opPattern","COPY",FACE,{"derivedFrom":subQ1,"instanceName":"87"}),makeQuery(id+"F3.opPattern","COPY",FACE,{"derivedFrom":subQ1,"instanceName":"88"}),makeQuery(id+"F3.opPattern","COPY",FACE,{"derivedFrom":subQ1,"instanceName":"89"}),makeQuery(id+"F3.opPattern","COPY",FACE,{"derivedFrom":subQ1,"instanceName":"90"}),makeQuery(id+"F3.opPattern","COPY",FACE,{"derivedFrom":subQ1,"instanceName":"91"}),makeQuery(id+"F3.opPattern","COPY",FACE,{"derivedFrom":subQ1,"instanceName":"92"}),makeQuery(id+"F3.opPattern","COPY",FACE,{"derivedFrom":subQ1,"instanceName":"93"}),makeQuery(id+"F3.opPattern","COPY",FACE,{"derivedFrom":subQ1,"instanceName":"94"}),makeQuery(id+"F3.opPattern","COPY",FACE,{"derivedFrom":subQ1,"instanceName":"95"}),makeQuery(id+"F3.opPattern","COPY",FACE,{"derivedFrom":subQ1,"instanceName":"96"}),makeQuery(id+"F3.opPattern","COPY",FACE,{"derivedFrom":subQ1,"instanceName":"97"}),makeQuery(id+"F3.opPattern","COPY",FACE,{"derivedFrom":subQ1,"instanceName":"98"}),makeQuery(id+"F3.opPattern","COPY",FACE,{"derivedFrom":subQ1,"instanceName":"99"}),makeQuery(id+"F3.opPattern","COPY",FACE,{"derivedFrom":subQ1,"instanceName":"100"}),makeQuery(id+"F3.opPattern","COPY",FACE,{"derivedFrom":subQ1,"instanceName":"101"}),makeQuery(id+"F3.opPattern","COPY",FACE,{"derivedFrom":subQ1,"instanceName":"102"}),makeQuery(id+"F3.opPattern","COPY",FACE,{"derivedFrom":subQ1,"instanceName":"103"}),makeQuery(id+"F3.opPattern","COPY",FACE,{"derivedFrom":subQ1,"instanceName":"104"}),makeQuery(id+"F3.opPattern","COPY",FACE,{"derivedFrom":subQ1,"instanceName":"105"}),makeQuery(id+"F3.opPattern","COPY",FACE,{"derivedFrom":subQ1,"instanceName":"106"}),makeQuery(id+"F3.opPattern","COPY",FACE,{"derivedFrom":subQ1,"instanceName":"107"}),makeQuery(id+"F3.opPattern","COPY",FACE,{"derivedFrom":subQ1,"instanceName":"108"}),makeQuery(id+"F3.opPattern","COPY",FACE,{"derivedFrom":subQ1,"instanceName":"109"}),makeQuery(id+"F3.opPattern","COPY",FACE,{"derivedFrom":subQ1,"instanceName":"110"}),makeQuery(id+"F3.opPattern","COPY",FACE,{"derivedFrom":subQ1,"instanceName":"111"}),makeQuery(id+"F3.opPattern","COPY",FACE,{"derivedFrom":subQ1,"instanceName":"112"}),makeQuery(id+"F3.opPattern","COPY",FACE,{"derivedFrom":subQ1,"instanceName":"113"}),makeQuery(id+"F3.opPattern","COPY",FACE,{"derivedFrom":subQ1,"instanceName":"114"}),makeQuery(id+"F3.opPattern","COPY",FACE,{"derivedFrom":subQ1,"instanceName":"115"}),makeQuery(id+"F3.opPattern","COPY",FACE,{"derivedFrom":subQ1,"instanceName":"116"}),makeQuery(id+"F3.opPattern","COPY",FACE,{"derivedFrom":subQ1,"instanceName":"117"}),makeQuery(id+"F3.opPattern","COPY",FACE,{"derivedFrom":subQ1,"instanceName":"118"}),makeQuery(id+"F3.opPattern","COPY",FACE,{"derivedFrom":subQ1,"instanceName":"119"}),makeQuery(id+"F3.opPattern","COPY",FACE,{"derivedFrom":subQ1,"instanceName":"120"}),makeQuery(id+"F3.opPattern","COPY",FACE,{"derivedFrom":subQ1,"instanceName":"121"}),makeQuery(id+"F3.opPattern","COPY",FACE,{"derivedFrom":subQ1,"instanceName":"122"}),makeQuery(id+"F3.opPattern","COPY",FACE,{"derivedFrom":subQ1,"instanceName":"123"}),makeQuery(id+"F3.opPattern","COPY",FACE,{"derivedFrom":subQ1,"instanceName":"124"}),makeQuery(id+"F3.opPattern","COPY",FACE,{"derivedFrom":subQ1,"instanceName":"125"}),makeQuery(id+"F3.opPattern","COPY",FACE,{"derivedFrom":subQ1,"instanceName":"126"}),makeQuery(id+"F3.opPattern","COPY",FACE,{"derivedFrom":subQ1,"instanceName":"127"}),makeQuery(id+"F3.opPattern","COPY",FACE,{"derivedFrom":subQ1,"instanceName":"128"}),makeQuery(id+"F3.opPattern","COPY",FACE,{"derivedFrom":subQ1,"instanceName":"129"}),makeQuery(id+"F3.opPattern","COPY",FACE,{"derivedFrom":subQ1,"instanceName":"130"}),makeQuery(id+"F3.opPattern","COPY",FACE,{"derivedFrom":subQ1,"instanceName":"131"})]});}
            extrude(context, id + "F7", {"entities" : qUnion([Q0, Q1]), "endBound" : BoundingType.UP_TO_SURFACE, "oppositeDirection" : true, "endBoundEntityFace" : qUnion([Q2]), "depth" : 25.4 * mm});
        }
        {
            var Q0;
            Q0=makeQuery(id+"F7.opExtrude","SWEPT_EDGE",EDGE,{"disambiguationData":[OSD([sQuery(id+"F6.wireOp",EDGE,"E16"),sQuery(id+"F6.wireOp",EDGE,"E21.0")])]});
            var Q1;
            Q1=makeQuery(id+"F7.opExtrude","SWEPT_EDGE",EDGE,{"disambiguationData":[OSD([sQuery(id+"F6.wireOp",EDGE,"E17"),sQuery(id+"F6.wireOp",EDGE,"E21.0")])]});
            var Q2;
            Q2=makeQuery(id+"F7.opExtrude","SWEPT_EDGE",EDGE,{"disambiguationData":[OSD([sQuery(id+"F6.wireOp",EDGE,"E17"),sQuery(id+"F6.wireOp",EDGE,"E22.0")])]});
            var Q3;
            Q3=makeQuery(id+"F7.opExtrude","SWEPT_EDGE",EDGE,{"disambiguationData":[OSD([sQuery(id+"F6.wireOp",EDGE,"E16"),sQuery(id+"F6.wireOp",EDGE,"E22.0")])]});
            fillet(context, id + "F8", {"entities" : qUnion([Q0, Q1, Q2, Q3]), "radius" : 6.35 * mm, "tangentPropagation" : true, "allowEdgeOverflow" : false});
        }
        {
            var Q0;
            Q0=makeQuery(id+"F7.opExtrude","SWEPT_BODY",BODY,{"disambiguationData":[OSD([sQuery(id+"F6.wireOp",EDGE,"E16"),sQuery(id+"F6.wireOp",EDGE,"E17"),sQuery(id+"F6.wireOp",EDGE,"E21.0"),sQuery(id+"F6.wireOp",EDGE,"E22.0")])]});
            var Q1;
            Q1=makeQuery(id+"F5.boolean.opBoolean","COPY",FACE,{"derivedFrom":makeQuery(id+"F5.opExtrude","SWEPT_FACE",FACE,{"disambiguationData":[OSD([sQuery(id+"F4.wireOp",EDGE,"E8")])]})});
            circularPattern(context, id + "F9", {"operationType" : NewBodyOperationType.REMOVE, "entities" : qUnion([Q0]), "axis" : qUnion([Q1]), "angle" : 360 * degree, "instanceCount" : 6, "equalSpace" : true});
        }
        {
            var Q0;
            {var subQ0=sQuery(id+"F0.wireOp",EDGE,"E7");var subQ1=makeQuery(id+"F2.opExtrude","CAP_FACE",FACE,{"disambiguationData":[OSD([sQuery(id+"F0.wireOp",EDGE,"E2"),sQuery(id+"F0.wireOp",EDGE,"E3"),sQuery(id+"F0.wireOp",EDGE,"E4"),sQuery(id+"F0.wireOp",EDGE,"E5"),sQuery(id+"F0.wireOp",EDGE,"E6"),subQ0])],"isStart":false});Q0=makeQuery(id+"F3.boolean.opBoolean","MERGE",FACE,{"derivedFrom":[makeQuery(id+"F1.opExtrude","CAP_FACE",FACE,{"disambiguationData":[OSD([sQuery(id+"F0.wireOp",EDGE,"E0"),sQuery(id+"F0.wireOp",EDGE,"E1"),subQ0])],"isStart":false}),subQ1,makeQuery(id+"F3.opPattern","COPY",FACE,{"derivedFrom":subQ1,"instanceName":"1"}),makeQuery(id+"F3.opPattern","COPY",FACE,{"derivedFrom":subQ1,"instanceName":"2"}),makeQuery(id+"F3.opPattern","COPY",FACE,{"derivedFrom":subQ1,"instanceName":"3"}),makeQuery(id+"F3.opPattern","COPY",FACE,{"derivedFrom":subQ1,"instanceName":"4"}),makeQuery(id+"F3.opPattern","COPY",FACE,{"derivedFrom":subQ1,"instanceName":"5"}),makeQuery(id+"F3.opPattern","COPY",FACE,{"derivedFrom":subQ1,"instanceName":"6"}),makeQuery(id+"F3.opPattern","COPY",FACE,{"derivedFrom":subQ1,"instanceName":"7"}),makeQuery(id+"F3.opPattern","COPY",FACE,{"derivedFrom":subQ1,"instanceName":"8"}),makeQuery(id+"F3.opPattern","COPY",FACE,{"derivedFrom":subQ1,"instanceName":"9"}),makeQuery(id+"F3.opPattern","COPY",FACE,{"derivedFrom":subQ1,"instanceName":"10"}),makeQuery(id+"F3.opPattern","COPY",FACE,{"derivedFrom":subQ1,"instanceName":"11"}),makeQuery(id+"F3.opPattern","COPY",FACE,{"derivedFrom":subQ1,"instanceName":"12"}),makeQuery(id+"F3.opPattern","COPY",FACE,{"derivedFrom":subQ1,"instanceName":"13"}),makeQuery(id+"F3.opPattern","COPY",FACE,{"derivedFrom":subQ1,"instanceName":"14"}),makeQuery(id+"F3.opPattern","COPY",FACE,{"derivedFrom":subQ1,"instanceName":"15"}),makeQuery(id+"F3.opPattern","COPY",FACE,{"derivedFrom":subQ1,"instanceName":"16"}),makeQuery(id+"F3.opPattern","COPY",FACE,{"derivedFrom":subQ1,"instanceName":"17"}),makeQuery(id+"F3.opPattern","COPY",FACE,{"derivedFrom":subQ1,"instanceName":"18"}),makeQuery(id+"F3.opPattern","COPY",FACE,{"derivedFrom":subQ1,"instanceName":"19"}),makeQuery(id+"F3.opPattern","COPY",FACE,{"derivedFrom":subQ1,"instanceName":"20"}),makeQuery(id+"F3.opPattern","COPY",FACE,{"derivedFrom":subQ1,"instanceName":"21"}),makeQuery(id+"F3.opPattern","COPY",FACE,{"derivedFrom":subQ1,"instanceName":"22"}),makeQuery(id+"F3.opPattern","COPY",FACE,{"derivedFrom":subQ1,"instanceName":"23"}),makeQuery(id+"F3.opPattern","COPY",FACE,{"derivedFrom":subQ1,"instanceName":"24"}),makeQuery(id+"F3.opPattern","COPY",FACE,{"derivedFrom":subQ1,"instanceName":"25"}),makeQuery(id+"F3.opPattern","COPY",FACE,{"derivedFrom":subQ1,"instanceName":"26"}),makeQuery(id+"F3.opPattern","COPY",FACE,{"derivedFrom":subQ1,"instanceName":"27"}),makeQuery(id+"F3.opPattern","COPY",FACE,{"derivedFrom":subQ1,"instanceName":"28"}),makeQuery(id+"F3.opPattern","COPY",FACE,{"derivedFrom":subQ1,"instanceName":"29"}),makeQuery(id+"F3.opPattern","COPY",FACE,{"derivedFrom":subQ1,"instanceName":"30"}),makeQuery(id+"F3.opPattern","COPY",FACE,{"derivedFrom":subQ1,"instanceName":"31"}),makeQuery(id+"F3.opPattern","COPY",FACE,{"derivedFrom":subQ1,"instanceName":"32"}),makeQuery(id+"F3.opPattern","COPY",FACE,{"derivedFrom":subQ1,"instanceName":"33"}),makeQuery(id+"F3.opPattern","COPY",FACE,{"derivedFrom":subQ1,"instanceName":"34"}),makeQuery(id+"F3.opPattern","COPY",FACE,{"derivedFrom":subQ1,"instanceName":"35"}),makeQuery(id+"F3.opPattern","COPY",FACE,{"derivedFrom":subQ1,"instanceName":"36"}),makeQuery(id+"F3.opPattern","COPY",FACE,{"derivedFrom":subQ1,"instanceName":"37"}),makeQuery(id+"F3.opPattern","COPY",FACE,{"derivedFrom":subQ1,"instanceName":"38"}),makeQuery(id+"F3.opPattern","COPY",FACE,{"derivedFrom":subQ1,"instanceName":"39"}),makeQuery(id+"F3.opPattern","COPY",FACE,{"derivedFrom":subQ1,"instanceName":"40"}),makeQuery(id+"F3.opPattern","COPY",FACE,{"derivedFrom":subQ1,"instanceName":"41"}),makeQuery(id+"F3.opPattern","COPY",FACE,{"derivedFrom":subQ1,"instanceName":"42"}),makeQuery(id+"F3.opPattern","COPY",FACE,{"derivedFrom":subQ1,"instanceName":"43"}),makeQuery(id+"F3.opPattern","COPY",FACE,{"derivedFrom":subQ1,"instanceName":"44"}),makeQuery(id+"F3.opPattern","COPY",FACE,{"derivedFrom":subQ1,"instanceName":"45"}),makeQuery(id+"F3.opPattern","COPY",FACE,{"derivedFrom":subQ1,"instanceName":"46"}),makeQuery(id+"F3.opPattern","COPY",FACE,{"derivedFrom":subQ1,"instanceName":"47"}),makeQuery(id+"F3.opPattern","COPY",FACE,{"derivedFrom":subQ1,"instanceName":"48"}),makeQuery(id+"F3.opPattern","COPY",FACE,{"derivedFrom":subQ1,"instanceName":"49"}),makeQuery(id+"F3.opPattern","COPY",FACE,{"derivedFrom":subQ1,"instanceName":"50"}),makeQuery(id+"F3.opPattern","COPY",FACE,{"derivedFrom":subQ1,"instanceName":"51"}),makeQuery(id+"F3.opPattern","COPY",FACE,{"derivedFrom":subQ1,"instanceName":"52"}),makeQuery(id+"F3.opPattern","COPY",FACE,{"derivedFrom":subQ1,"instanceName":"53"}),makeQuery(id+"F3.opPattern","COPY",FACE,{"derivedFrom":subQ1,"instanceName":"54"}),makeQuery(id+"F3.opPattern","COPY",FACE,{"derivedFrom":subQ1,"instanceName":"55"}),makeQuery(id+"F3.opPattern","COPY",FACE,{"derivedFrom":subQ1,"instanceName":"56"}),makeQuery(id+"F3.opPattern","COPY",FACE,{"derivedFrom":subQ1,"instanceName":"57"}),makeQuery(id+"F3.opPattern","COPY",FACE,{"derivedFrom":subQ1,"instanceName":"58"}),makeQuery(id+"F3.opPattern","COPY",FACE,{"derivedFrom":subQ1,"instanceName":"59"}),makeQuery(id+"F3.opPattern","COPY",FACE,{"derivedFrom":subQ1,"instanceName":"60"}),makeQuery(id+"F3.opPattern","COPY",FACE,{"derivedFrom":subQ1,"instanceName":"61"}),makeQuery(id+"F3.opPattern","COPY",FACE,{"derivedFrom":subQ1,"instanceName":"62"}),makeQuery(id+"F3.opPattern","COPY",FACE,{"derivedFrom":subQ1,"instanceName":"63"}),makeQuery(id+"F3.opPattern","COPY",FACE,{"derivedFrom":subQ1,"instanceName":"64"}),makeQuery(id+"F3.opPattern","COPY",FACE,{"derivedFrom":subQ1,"instanceName":"65"}),makeQuery(id+"F3.opPattern","COPY",FACE,{"derivedFrom":subQ1,"instanceName":"66"}),makeQuery(id+"F3.opPattern","COPY",FACE,{"derivedFrom":subQ1,"instanceName":"67"}),makeQuery(id+"F3.opPattern","COPY",FACE,{"derivedFrom":subQ1,"instanceName":"68"}),makeQuery(id+"F3.opPattern","COPY",FACE,{"derivedFrom":subQ1,"instanceName":"69"}),makeQuery(id+"F3.opPattern","COPY",FACE,{"derivedFrom":subQ1,"instanceName":"70"}),makeQuery(id+"F3.opPattern","COPY",FACE,{"derivedFrom":subQ1,"instanceName":"71"}),makeQuery(id+"F3.opPattern","COPY",FACE,{"derivedFrom":subQ1,"instanceName":"72"}),makeQuery(id+"F3.opPattern","COPY",FACE,{"derivedFrom":subQ1,"instanceName":"73"}),makeQuery(id+"F3.opPattern","COPY",FACE,{"derivedFrom":subQ1,"instanceName":"74"}),makeQuery(id+"F3.opPattern","COPY",FACE,{"derivedFrom":subQ1,"instanceName":"75"}),makeQuery(id+"F3.opPattern","COPY",FACE,{"derivedFrom":subQ1,"instanceName":"76"}),makeQuery(id+"F3.opPattern","COPY",FACE,{"derivedFrom":subQ1,"instanceName":"77"}),makeQuery(id+"F3.opPattern","COPY",FACE,{"derivedFrom":subQ1,"instanceName":"78"}),makeQuery(id+"F3.opPattern","COPY",FACE,{"derivedFrom":subQ1,"instanceName":"79"}),makeQuery(id+"F3.opPattern","COPY",FACE,{"derivedFrom":subQ1,"instanceName":"80"}),makeQuery(id+"F3.opPattern","COPY",FACE,{"derivedFrom":subQ1,"instanceName":"81"}),makeQuery(id+"F3.opPattern","COPY",FACE,{"derivedFrom":subQ1,"instanceName":"82"}),makeQuery(id+"F3.opPattern","COPY",FACE,{"derivedFrom":subQ1,"instanceName":"83"}),makeQuery(id+"F3.opPattern","COPY",FACE,{"derivedFrom":subQ1,"instanceName":"84"}),makeQuery(id+"F3.opPattern","COPY",FACE,{"derivedFrom":subQ1,"instanceName":"85"}),makeQuery(id+"F3.opPattern","COPY",FACE,{"derivedFrom":subQ1,"instanceName":"86"}),makeQuery(id+"F3.opPattern","COPY",FACE,{"derivedFrom":subQ1,"instanceName":"87"}),makeQuery(id+"F3.opPattern","COPY",FACE,{"derivedFrom":subQ1,"instanceName":"88"}),makeQuery(id+"F3.opPattern","COPY",FACE,{"derivedFrom":subQ1,"instanceName":"89"}),makeQuery(id+"F3.opPattern","COPY",FACE,{"derivedFrom":subQ1,"instanceName":"90"}),makeQuery(id+"F3.opPattern","COPY",FACE,{"derivedFrom":subQ1,"instanceName":"91"}),makeQuery(id+"F3.opPattern","COPY",FACE,{"derivedFrom":subQ1,"instanceName":"92"}),makeQuery(id+"F3.opPattern","COPY",FACE,{"derivedFrom":subQ1,"instanceName":"93"}),makeQuery(id+"F3.opPattern","COPY",FACE,{"derivedFrom":subQ1,"instanceName":"94"}),makeQuery(id+"F3.opPattern","COPY",FACE,{"derivedFrom":subQ1,"instanceName":"95"}),makeQuery(id+"F3.opPattern","COPY",FACE,{"derivedFrom":subQ1,"instanceName":"96"}),makeQuery(id+"F3.opPattern","COPY",FACE,{"derivedFrom":subQ1,"instanceName":"97"}),makeQuery(id+"F3.opPattern","COPY",FACE,{"derivedFrom":subQ1,"instanceName":"98"}),makeQuery(id+"F3.opPattern","COPY",FACE,{"derivedFrom":subQ1,"instanceName":"99"}),makeQuery(id+"F3.opPattern","COPY",FACE,{"derivedFrom":subQ1,"instanceName":"100"}),makeQuery(id+"F3.opPattern","COPY",FACE,{"derivedFrom":subQ1,"instanceName":"101"}),makeQuery(id+"F3.opPattern","COPY",FACE,{"derivedFrom":subQ1,"instanceName":"102"}),makeQuery(id+"F3.opPattern","COPY",FACE,{"derivedFrom":subQ1,"instanceName":"103"}),makeQuery(id+"F3.opPattern","COPY",FACE,{"derivedFrom":subQ1,"instanceName":"104"}),makeQuery(id+"F3.opPattern","COPY",FACE,{"derivedFrom":subQ1,"instanceName":"105"}),makeQuery(id+"F3.opPattern","COPY",FACE,{"derivedFrom":subQ1,"instanceName":"106"}),makeQuery(id+"F3.opPattern","COPY",FACE,{"derivedFrom":subQ1,"instanceName":"107"}),makeQuery(id+"F3.opPattern","COPY",FACE,{"derivedFrom":subQ1,"instanceName":"108"}),makeQuery(id+"F3.opPattern","COPY",FACE,{"derivedFrom":subQ1,"instanceName":"109"}),makeQuery(id+"F3.opPattern","COPY",FACE,{"derivedFrom":subQ1,"instanceName":"110"}),makeQuery(id+"F3.opPattern","COPY",FACE,{"derivedFrom":subQ1,"instanceName":"111"}),makeQuery(id+"F3.opPattern","COPY",FACE,{"derivedFrom":subQ1,"instanceName":"112"}),makeQuery(id+"F3.opPattern","COPY",FACE,{"derivedFrom":subQ1,"instanceName":"113"}),makeQuery(id+"F3.opPattern","COPY",FACE,{"derivedFrom":subQ1,"instanceName":"114"}),makeQuery(id+"F3.opPattern","COPY",FACE,{"derivedFrom":subQ1,"instanceName":"115"}),makeQuery(id+"F3.opPattern","COPY",FACE,{"derivedFrom":subQ1,"instanceName":"116"}),makeQuery(id+"F3.opPattern","COPY",FACE,{"derivedFrom":subQ1,"instanceName":"117"}),makeQuery(id+"F3.opPattern","COPY",FACE,{"derivedFrom":subQ1,"instanceName":"118"}),makeQuery(id+"F3.opPattern","COPY",FACE,{"derivedFrom":subQ1,"instanceName":"119"}),makeQuery(id+"F3.opPattern","COPY",FACE,{"derivedFrom":subQ1,"instanceName":"120"}),makeQuery(id+"F3.opPattern","COPY",FACE,{"derivedFrom":subQ1,"instanceName":"121"}),makeQuery(id+"F3.opPattern","COPY",FACE,{"derivedFrom":subQ1,"instanceName":"122"}),makeQuery(id+"F3.opPattern","COPY",FACE,{"derivedFrom":subQ1,"instanceName":"123"}),makeQuery(id+"F3.opPattern","COPY",FACE,{"derivedFrom":subQ1,"instanceName":"124"}),makeQuery(id+"F3.opPattern","COPY",FACE,{"derivedFrom":subQ1,"instanceName":"125"}),makeQuery(id+"F3.opPattern","COPY",FACE,{"derivedFrom":subQ1,"instanceName":"126"}),makeQuery(id+"F3.opPattern","COPY",FACE,{"derivedFrom":subQ1,"instanceName":"127"}),makeQuery(id+"F3.opPattern","COPY",FACE,{"derivedFrom":subQ1,"instanceName":"128"}),makeQuery(id+"F3.opPattern","COPY",FACE,{"derivedFrom":subQ1,"instanceName":"129"}),makeQuery(id+"F3.opPattern","COPY",FACE,{"derivedFrom":subQ1,"instanceName":"130"}),makeQuery(id+"F3.opPattern","COPY",FACE,{"derivedFrom":subQ1,"instanceName":"131"})]});}
            var sketch = newSketch(context, id + "F10", { "sketchPlane" : qUnion([Q0])});
            skArc(sketch, "E27", {"start": v(-10.66, 28.02) * mm, "mid": v(-14.99, 25.96) * mm, "end": v(-18.93, 23.24) * mm});
            skArc(sketch, "E28.0", {"start": v(18.93, 23.24) * mm, "mid": v(19.25, 11.11) * mm, "end": v(29.6, 4.78) * mm});
            skArc(sketch, "E29.0", {"start": v(-10.66, 28.02) * mm, "mid": v(0, 22.23) * mm, "end": v(10.66, 28.02) * mm});
            skArc(sketch, "E29.1", {"start": v(-29.78, 4.77) * mm, "mid": v(-19.25, 11.11) * mm, "end": v(-19.02, 23.4) * mm});
            skArc(sketch, "E29.2", {"start": v(-18.93, -23.24) * mm, "mid": v(-19.25, -11.11) * mm, "end": v(-29.6, -4.78) * mm});
            skArc(sketch, "E29.3", {"start": v(10.66, -28.02) * mm, "mid": v(0, -22.23) * mm, "end": v(-10.66, -28.02) * mm});
            skArc(sketch, "E29.4", {"start": v(29.6, -4.78) * mm, "mid": v(19.25, -11.11) * mm, "end": v(18.93, -23.24) * mm});
            skArc(sketch, "E30.trimOffspring", {"start": v(18.93, 23.24) * mm, "mid": v(14.99, 25.96) * mm, "end": v(10.66, 28.02) * mm});
            skArc(sketch, "E31.trimOffspring", {"start": v(29.6, -4.78) * mm, "mid": v(29.97, 0) * mm, "end": v(29.6, 4.78) * mm});
            skArc(sketch, "E32.trimOffspring", {"start": v(10.66, -28.02) * mm, "mid": v(14.99, -25.96) * mm, "end": v(18.93, -23.24) * mm});
            skArc(sketch, "E33.trimOffspring", {"start": v(-18.93, -23.24) * mm, "mid": v(-14.99, -25.96) * mm, "end": v(-10.66, -28.02) * mm});
            skArc(sketch, "E34.trimOffspring", {"start": v(-29.6, 4.78) * mm, "mid": v(-29.97, 0) * mm, "end": v(-29.6, -4.78) * mm});
            skCircle(sketch, "E35.0", {"center": v(-11.9, 20.62) * mm, "radius": 2.41 * mm});
            skCircle(sketch, "E35.1", {"center": v(11.9, 20.62) * mm, "radius": 2.41 * mm});
            skCircle(sketch, "E35.2", {"center": v(23.81, 0) * mm, "radius": 2.41 * mm});
            skCircle(sketch, "E35.3", {"center": v(11.9, -20.62) * mm, "radius": 2.41 * mm});
            skCircle(sketch, "E35.4", {"center": v(-11.9, -20.62) * mm, "radius": 2.41 * mm});
            skCircle(sketch, "E35.5", {"center": v(-23.81, 0) * mm, "radius": 2.41 * mm});
            skCircle(sketch, "E36.0", {"center": v(0, 0) * mm, "radius": 14.29 * mm});
            skSolve(sketch);
        }
        {
            var Q0;
            Q0=qSketchRegion(id+"F10",true);
            extrude(context, id + "F11", {"entities" : qUnion([Q0]), "depth" : 3.17 * mm});
        }
        {
            var Q0;
            Q0=makeQuery(id+"F11.opExtrude","SWEPT_EDGE",EDGE,{"disambiguationData":[OSD([sQuery(id+"F6.wireOp",EDGE,"E16"),sQuery(id+"F6.wireOp",EDGE,"E17"),sQuery(id+"F6.wireOp",EDGE,"E21.0"),sQuery(id+"F6.wireOp",EDGE,"E22.0"),sQuery(id+"F6.wireOp",EDGE,"E24"),sQuery(id+"F10.wireOp",EDGE,"E28.0"),sQuery(id+"F10.wireOp",EDGE,"E30.trimOffspring")])]});
            var Q1;
            Q1=makeQuery(id+"F11.opExtrude","SWEPT_EDGE",EDGE,{"disambiguationData":[OSD([sQuery(id+"F6.wireOp",EDGE,"E16"),sQuery(id+"F6.wireOp",EDGE,"E17"),sQuery(id+"F6.wireOp",EDGE,"E21.0"),sQuery(id+"F6.wireOp",EDGE,"E22.0"),sQuery(id+"F6.wireOp",EDGE,"E24"),sQuery(id+"F10.wireOp",EDGE,"E28.0"),sQuery(id+"F10.wireOp",EDGE,"E31.trimOffspring")])]});
            var Q2;
            Q2=makeQuery(id+"F11.opExtrude","SWEPT_EDGE",EDGE,{"disambiguationData":[OSD([sQuery(id+"F6.wireOp",EDGE,"E16"),sQuery(id+"F6.wireOp",EDGE,"E17"),sQuery(id+"F6.wireOp",EDGE,"E21.0"),sQuery(id+"F6.wireOp",EDGE,"E22.0"),sQuery(id+"F6.wireOp",EDGE,"E24"),sQuery(id+"F10.wireOp",EDGE,"E29.4"),sQuery(id+"F10.wireOp",EDGE,"E31.trimOffspring")])]});
            var Q3;
            Q3=makeQuery(id+"F11.opExtrude","SWEPT_EDGE",EDGE,{"disambiguationData":[OSD([sQuery(id+"F6.wireOp",EDGE,"E16"),sQuery(id+"F6.wireOp",EDGE,"E17"),sQuery(id+"F6.wireOp",EDGE,"E21.0"),sQuery(id+"F6.wireOp",EDGE,"E22.0"),sQuery(id+"F6.wireOp",EDGE,"E24"),sQuery(id+"F10.wireOp",EDGE,"E29.4"),sQuery(id+"F10.wireOp",EDGE,"E32.trimOffspring")])]});
            var Q4;
            Q4=makeQuery(id+"F11.opExtrude","SWEPT_EDGE",EDGE,{"disambiguationData":[OSD([sQuery(id+"F6.wireOp",EDGE,"E16"),sQuery(id+"F6.wireOp",EDGE,"E17"),sQuery(id+"F6.wireOp",EDGE,"E21.0"),sQuery(id+"F6.wireOp",EDGE,"E22.0"),sQuery(id+"F6.wireOp",EDGE,"E24"),sQuery(id+"F10.wireOp",EDGE,"E29.3"),sQuery(id+"F10.wireOp",EDGE,"E32.trimOffspring")])]});
            var Q5;
            Q5=makeQuery(id+"F11.opExtrude","SWEPT_EDGE",EDGE,{"disambiguationData":[OSD([sQuery(id+"F6.wireOp",EDGE,"E16"),sQuery(id+"F6.wireOp",EDGE,"E17"),sQuery(id+"F6.wireOp",EDGE,"E21.0"),sQuery(id+"F6.wireOp",EDGE,"E22.0"),sQuery(id+"F6.wireOp",EDGE,"E24"),sQuery(id+"F10.wireOp",EDGE,"E29.3"),sQuery(id+"F10.wireOp",EDGE,"E33.trimOffspring")])]});
            var Q6;
            Q6=makeQuery(id+"F11.opExtrude","SWEPT_EDGE",EDGE,{"disambiguationData":[OSD([sQuery(id+"F6.wireOp",EDGE,"E16"),sQuery(id+"F6.wireOp",EDGE,"E17"),sQuery(id+"F6.wireOp",EDGE,"E21.0"),sQuery(id+"F6.wireOp",EDGE,"E22.0"),sQuery(id+"F6.wireOp",EDGE,"E24"),sQuery(id+"F10.wireOp",EDGE,"E29.2"),sQuery(id+"F10.wireOp",EDGE,"E33.trimOffspring")])]});
            var Q7;
            Q7=makeQuery(id+"F11.opExtrude","SWEPT_EDGE",EDGE,{"disambiguationData":[OSD([sQuery(id+"F6.wireOp",EDGE,"E16"),sQuery(id+"F6.wireOp",EDGE,"E17"),sQuery(id+"F6.wireOp",EDGE,"E21.0"),sQuery(id+"F6.wireOp",EDGE,"E22.0"),sQuery(id+"F6.wireOp",EDGE,"E24"),sQuery(id+"F10.wireOp",EDGE,"E29.2"),sQuery(id+"F10.wireOp",EDGE,"E34.trimOffspring")])]});
            var Q8;
            Q8=makeQuery(id+"F11.opExtrude","SWEPT_EDGE",EDGE,{"disambiguationData":[OSD([sQuery(id+"F6.wireOp",EDGE,"E16"),sQuery(id+"F6.wireOp",EDGE,"E17"),sQuery(id+"F6.wireOp",EDGE,"E21.0"),sQuery(id+"F6.wireOp",EDGE,"E22.0"),sQuery(id+"F6.wireOp",EDGE,"E24"),sQuery(id+"F10.wireOp",EDGE,"E29.1"),sQuery(id+"F10.wireOp",EDGE,"E34.trimOffspring")])]});
            var Q9;
            Q9=makeQuery(id+"F11.opExtrude","SWEPT_EDGE",EDGE,{"disambiguationData":[OSD([sQuery(id+"F6.wireOp",EDGE,"E16"),sQuery(id+"F6.wireOp",EDGE,"E17"),sQuery(id+"F6.wireOp",EDGE,"E21.0"),sQuery(id+"F6.wireOp",EDGE,"E22.0"),sQuery(id+"F6.wireOp",EDGE,"E24"),sQuery(id+"F10.wireOp",EDGE,"E27"),sQuery(id+"F10.wireOp",EDGE,"E29.1")])]});
            var Q10;
            Q10=makeQuery(id+"F11.opExtrude","SWEPT_EDGE",EDGE,{"disambiguationData":[OSD([sQuery(id+"F6.wireOp",EDGE,"E16"),sQuery(id+"F6.wireOp",EDGE,"E17"),sQuery(id+"F6.wireOp",EDGE,"E21.0"),sQuery(id+"F6.wireOp",EDGE,"E22.0"),sQuery(id+"F6.wireOp",EDGE,"E24"),sQuery(id+"F10.wireOp",EDGE,"E27"),sQuery(id+"F10.wireOp",EDGE,"E29.0")])]});
            var Q11;
            Q11=makeQuery(id+"F11.opExtrude","SWEPT_EDGE",EDGE,{"disambiguationData":[OSD([sQuery(id+"F6.wireOp",EDGE,"E16"),sQuery(id+"F6.wireOp",EDGE,"E17"),sQuery(id+"F6.wireOp",EDGE,"E21.0"),sQuery(id+"F6.wireOp",EDGE,"E22.0"),sQuery(id+"F6.wireOp",EDGE,"E24"),sQuery(id+"F10.wireOp",EDGE,"E29.0"),sQuery(id+"F10.wireOp",EDGE,"E30.trimOffspring")])]});
            fillet(context, id + "F12", {"entities" : qUnion([Q0, Q1, Q2, Q3, Q4, Q5, Q6, Q7, Q8, Q9, Q10, Q11]), "radius" : 1.59 * mm, "tangentPropagation" : true, "allowEdgeOverflow" : false});
        }
        {
            var Q0;
            {var subQ0=sQuery(id+"F0.wireOp",EDGE,"E7");var subQ1=makeQuery(id+"F2.opExtrude","CAP_FACE",FACE,{"disambiguationData":[OSD([sQuery(id+"F0.wireOp",EDGE,"E2"),sQuery(id+"F0.wireOp",EDGE,"E3"),sQuery(id+"F0.wireOp",EDGE,"E4"),sQuery(id+"F0.wireOp",EDGE,"E5"),sQuery(id+"F0.wireOp",EDGE,"E6"),subQ0])],"isStart":true});Q0=makeQuery(id+"F3.boolean.opBoolean","MERGE",FACE,{"derivedFrom":[makeQuery(id+"F1.opExtrude","CAP_FACE",FACE,{"disambiguationData":[OSD([sQuery(id+"F0.wireOp",EDGE,"E0"),sQuery(id+"F0.wireOp",EDGE,"E1"),subQ0])],"isStart":true}),subQ1,makeQuery(id+"F3.opPattern","COPY",FACE,{"derivedFrom":subQ1,"instanceName":"1"}),makeQuery(id+"F3.opPattern","COPY",FACE,{"derivedFrom":subQ1,"instanceName":"2"}),makeQuery(id+"F3.opPattern","COPY",FACE,{"derivedFrom":subQ1,"instanceName":"3"}),makeQuery(id+"F3.opPattern","COPY",FACE,{"derivedFrom":subQ1,"instanceName":"4"}),makeQuery(id+"F3.opPattern","COPY",FACE,{"derivedFrom":subQ1,"instanceName":"5"}),makeQuery(id+"F3.opPattern","COPY",FACE,{"derivedFrom":subQ1,"instanceName":"6"}),makeQuery(id+"F3.opPattern","COPY",FACE,{"derivedFrom":subQ1,"instanceName":"7"}),makeQuery(id+"F3.opPattern","COPY",FACE,{"derivedFrom":subQ1,"instanceName":"8"}),makeQuery(id+"F3.opPattern","COPY",FACE,{"derivedFrom":subQ1,"instanceName":"9"}),makeQuery(id+"F3.opPattern","COPY",FACE,{"derivedFrom":subQ1,"instanceName":"10"}),makeQuery(id+"F3.opPattern","COPY",FACE,{"derivedFrom":subQ1,"instanceName":"11"}),makeQuery(id+"F3.opPattern","COPY",FACE,{"derivedFrom":subQ1,"instanceName":"12"}),makeQuery(id+"F3.opPattern","COPY",FACE,{"derivedFrom":subQ1,"instanceName":"13"}),makeQuery(id+"F3.opPattern","COPY",FACE,{"derivedFrom":subQ1,"instanceName":"14"}),makeQuery(id+"F3.opPattern","COPY",FACE,{"derivedFrom":subQ1,"instanceName":"15"}),makeQuery(id+"F3.opPattern","COPY",FACE,{"derivedFrom":subQ1,"instanceName":"16"}),makeQuery(id+"F3.opPattern","COPY",FACE,{"derivedFrom":subQ1,"instanceName":"17"}),makeQuery(id+"F3.opPattern","COPY",FACE,{"derivedFrom":subQ1,"instanceName":"18"}),makeQuery(id+"F3.opPattern","COPY",FACE,{"derivedFrom":subQ1,"instanceName":"19"}),makeQuery(id+"F3.opPattern","COPY",FACE,{"derivedFrom":subQ1,"instanceName":"20"}),makeQuery(id+"F3.opPattern","COPY",FACE,{"derivedFrom":subQ1,"instanceName":"21"}),makeQuery(id+"F3.opPattern","COPY",FACE,{"derivedFrom":subQ1,"instanceName":"22"}),makeQuery(id+"F3.opPattern","COPY",FACE,{"derivedFrom":subQ1,"instanceName":"23"}),makeQuery(id+"F3.opPattern","COPY",FACE,{"derivedFrom":subQ1,"instanceName":"24"}),makeQuery(id+"F3.opPattern","COPY",FACE,{"derivedFrom":subQ1,"instanceName":"25"}),makeQuery(id+"F3.opPattern","COPY",FACE,{"derivedFrom":subQ1,"instanceName":"26"}),makeQuery(id+"F3.opPattern","COPY",FACE,{"derivedFrom":subQ1,"instanceName":"27"}),makeQuery(id+"F3.opPattern","COPY",FACE,{"derivedFrom":subQ1,"instanceName":"28"}),makeQuery(id+"F3.opPattern","COPY",FACE,{"derivedFrom":subQ1,"instanceName":"29"}),makeQuery(id+"F3.opPattern","COPY",FACE,{"derivedFrom":subQ1,"instanceName":"30"}),makeQuery(id+"F3.opPattern","COPY",FACE,{"derivedFrom":subQ1,"instanceName":"31"}),makeQuery(id+"F3.opPattern","COPY",FACE,{"derivedFrom":subQ1,"instanceName":"32"}),makeQuery(id+"F3.opPattern","COPY",FACE,{"derivedFrom":subQ1,"instanceName":"33"}),makeQuery(id+"F3.opPattern","COPY",FACE,{"derivedFrom":subQ1,"instanceName":"34"}),makeQuery(id+"F3.opPattern","COPY",FACE,{"derivedFrom":subQ1,"instanceName":"35"}),makeQuery(id+"F3.opPattern","COPY",FACE,{"derivedFrom":subQ1,"instanceName":"36"}),makeQuery(id+"F3.opPattern","COPY",FACE,{"derivedFrom":subQ1,"instanceName":"37"}),makeQuery(id+"F3.opPattern","COPY",FACE,{"derivedFrom":subQ1,"instanceName":"38"}),makeQuery(id+"F3.opPattern","COPY",FACE,{"derivedFrom":subQ1,"instanceName":"39"}),makeQuery(id+"F3.opPattern","COPY",FACE,{"derivedFrom":subQ1,"instanceName":"40"}),makeQuery(id+"F3.opPattern","COPY",FACE,{"derivedFrom":subQ1,"instanceName":"41"}),makeQuery(id+"F3.opPattern","COPY",FACE,{"derivedFrom":subQ1,"instanceName":"42"}),makeQuery(id+"F3.opPattern","COPY",FACE,{"derivedFrom":subQ1,"instanceName":"43"}),makeQuery(id+"F3.opPattern","COPY",FACE,{"derivedFrom":subQ1,"instanceName":"44"}),makeQuery(id+"F3.opPattern","COPY",FACE,{"derivedFrom":subQ1,"instanceName":"45"}),makeQuery(id+"F3.opPattern","COPY",FACE,{"derivedFrom":subQ1,"instanceName":"46"}),makeQuery(id+"F3.opPattern","COPY",FACE,{"derivedFrom":subQ1,"instanceName":"47"}),makeQuery(id+"F3.opPattern","COPY",FACE,{"derivedFrom":subQ1,"instanceName":"48"}),makeQuery(id+"F3.opPattern","COPY",FACE,{"derivedFrom":subQ1,"instanceName":"49"}),makeQuery(id+"F3.opPattern","COPY",FACE,{"derivedFrom":subQ1,"instanceName":"50"}),makeQuery(id+"F3.opPattern","COPY",FACE,{"derivedFrom":subQ1,"instanceName":"51"}),makeQuery(id+"F3.opPattern","COPY",FACE,{"derivedFrom":subQ1,"instanceName":"52"}),makeQuery(id+"F3.opPattern","COPY",FACE,{"derivedFrom":subQ1,"instanceName":"53"}),makeQuery(id+"F3.opPattern","COPY",FACE,{"derivedFrom":subQ1,"instanceName":"54"}),makeQuery(id+"F3.opPattern","COPY",FACE,{"derivedFrom":subQ1,"instanceName":"55"}),makeQuery(id+"F3.opPattern","COPY",FACE,{"derivedFrom":subQ1,"instanceName":"56"}),makeQuery(id+"F3.opPattern","COPY",FACE,{"derivedFrom":subQ1,"instanceName":"57"}),makeQuery(id+"F3.opPattern","COPY",FACE,{"derivedFrom":subQ1,"instanceName":"58"}),makeQuery(id+"F3.opPattern","COPY",FACE,{"derivedFrom":subQ1,"instanceName":"59"}),makeQuery(id+"F3.opPattern","COPY",FACE,{"derivedFrom":subQ1,"instanceName":"60"}),makeQuery(id+"F3.opPattern","COPY",FACE,{"derivedFrom":subQ1,"instanceName":"61"}),makeQuery(id+"F3.opPattern","COPY",FACE,{"derivedFrom":subQ1,"instanceName":"62"}),makeQuery(id+"F3.opPattern","COPY",FACE,{"derivedFrom":subQ1,"instanceName":"63"}),makeQuery(id+"F3.opPattern","COPY",FACE,{"derivedFrom":subQ1,"instanceName":"64"}),makeQuery(id+"F3.opPattern","COPY",FACE,{"derivedFrom":subQ1,"instanceName":"65"}),makeQuery(id+"F3.opPattern","COPY",FACE,{"derivedFrom":subQ1,"instanceName":"66"}),makeQuery(id+"F3.opPattern","COPY",FACE,{"derivedFrom":subQ1,"instanceName":"67"}),makeQuery(id+"F3.opPattern","COPY",FACE,{"derivedFrom":subQ1,"instanceName":"68"}),makeQuery(id+"F3.opPattern","COPY",FACE,{"derivedFrom":subQ1,"instanceName":"69"}),makeQuery(id+"F3.opPattern","COPY",FACE,{"derivedFrom":subQ1,"instanceName":"70"}),makeQuery(id+"F3.opPattern","COPY",FACE,{"derivedFrom":subQ1,"instanceName":"71"}),makeQuery(id+"F3.opPattern","COPY",FACE,{"derivedFrom":subQ1,"instanceName":"72"}),makeQuery(id+"F3.opPattern","COPY",FACE,{"derivedFrom":subQ1,"instanceName":"73"}),makeQuery(id+"F3.opPattern","COPY",FACE,{"derivedFrom":subQ1,"instanceName":"74"}),makeQuery(id+"F3.opPattern","COPY",FACE,{"derivedFrom":subQ1,"instanceName":"75"}),makeQuery(id+"F3.opPattern","COPY",FACE,{"derivedFrom":subQ1,"instanceName":"76"}),makeQuery(id+"F3.opPattern","COPY",FACE,{"derivedFrom":subQ1,"instanceName":"77"}),makeQuery(id+"F3.opPattern","COPY",FACE,{"derivedFrom":subQ1,"instanceName":"78"}),makeQuery(id+"F3.opPattern","COPY",FACE,{"derivedFrom":subQ1,"instanceName":"79"}),makeQuery(id+"F3.opPattern","COPY",FACE,{"derivedFrom":subQ1,"instanceName":"80"}),makeQuery(id+"F3.opPattern","COPY",FACE,{"derivedFrom":subQ1,"instanceName":"81"}),makeQuery(id+"F3.opPattern","COPY",FACE,{"derivedFrom":subQ1,"instanceName":"82"}),makeQuery(id+"F3.opPattern","COPY",FACE,{"derivedFrom":subQ1,"instanceName":"83"}),makeQuery(id+"F3.opPattern","COPY",FACE,{"derivedFrom":subQ1,"instanceName":"84"}),makeQuery(id+"F3.opPattern","COPY",FACE,{"derivedFrom":subQ1,"instanceName":"85"}),makeQuery(id+"F3.opPattern","COPY",FACE,{"derivedFrom":subQ1,"instanceName":"86"}),makeQuery(id+"F3.opPattern","COPY",FACE,{"derivedFrom":subQ1,"instanceName":"87"}),makeQuery(id+"F3.opPattern","COPY",FACE,{"derivedFrom":subQ1,"instanceName":"88"}),makeQuery(id+"F3.opPattern","COPY",FACE,{"derivedFrom":subQ1,"instanceName":"89"}),makeQuery(id+"F3.opPattern","COPY",FACE,{"derivedFrom":subQ1,"instanceName":"90"}),makeQuery(id+"F3.opPattern","COPY",FACE,{"derivedFrom":subQ1,"instanceName":"91"}),makeQuery(id+"F3.opPattern","COPY",FACE,{"derivedFrom":subQ1,"instanceName":"92"}),makeQuery(id+"F3.opPattern","COPY",FACE,{"derivedFrom":subQ1,"instanceName":"93"}),makeQuery(id+"F3.opPattern","COPY",FACE,{"derivedFrom":subQ1,"instanceName":"94"}),makeQuery(id+"F3.opPattern","COPY",FACE,{"derivedFrom":subQ1,"instanceName":"95"}),makeQuery(id+"F3.opPattern","COPY",FACE,{"derivedFrom":subQ1,"instanceName":"96"}),makeQuery(id+"F3.opPattern","COPY",FACE,{"derivedFrom":subQ1,"instanceName":"97"}),makeQuery(id+"F3.opPattern","COPY",FACE,{"derivedFrom":subQ1,"instanceName":"98"}),makeQuery(id+"F3.opPattern","COPY",FACE,{"derivedFrom":subQ1,"instanceName":"99"}),makeQuery(id+"F3.opPattern","COPY",FACE,{"derivedFrom":subQ1,"instanceName":"100"}),makeQuery(id+"F3.opPattern","COPY",FACE,{"derivedFrom":subQ1,"instanceName":"101"}),makeQuery(id+"F3.opPattern","COPY",FACE,{"derivedFrom":subQ1,"instanceName":"102"}),makeQuery(id+"F3.opPattern","COPY",FACE,{"derivedFrom":subQ1,"instanceName":"103"}),makeQuery(id+"F3.opPattern","COPY",FACE,{"derivedFrom":subQ1,"instanceName":"104"}),makeQuery(id+"F3.opPattern","COPY",FACE,{"derivedFrom":subQ1,"instanceName":"105"}),makeQuery(id+"F3.opPattern","COPY",FACE,{"derivedFrom":subQ1,"instanceName":"106"}),makeQuery(id+"F3.opPattern","COPY",FACE,{"derivedFrom":subQ1,"instanceName":"107"}),makeQuery(id+"F3.opPattern","COPY",FACE,{"derivedFrom":subQ1,"instanceName":"108"}),makeQuery(id+"F3.opPattern","COPY",FACE,{"derivedFrom":subQ1,"instanceName":"109"}),makeQuery(id+"F3.opPattern","COPY",FACE,{"derivedFrom":subQ1,"instanceName":"110"}),makeQuery(id+"F3.opPattern","COPY",FACE,{"derivedFrom":subQ1,"instanceName":"111"}),makeQuery(id+"F3.opPattern","COPY",FACE,{"derivedFrom":subQ1,"instanceName":"112"}),makeQuery(id+"F3.opPattern","COPY",FACE,{"derivedFrom":subQ1,"instanceName":"113"}),makeQuery(id+"F3.opPattern","COPY",FACE,{"derivedFrom":subQ1,"instanceName":"114"}),makeQuery(id+"F3.opPattern","COPY",FACE,{"derivedFrom":subQ1,"instanceName":"115"}),makeQuery(id+"F3.opPattern","COPY",FACE,{"derivedFrom":subQ1,"instanceName":"116"}),makeQuery(id+"F3.opPattern","COPY",FACE,{"derivedFrom":subQ1,"instanceName":"117"}),makeQuery(id+"F3.opPattern","COPY",FACE,{"derivedFrom":subQ1,"instanceName":"118"}),makeQuery(id+"F3.opPattern","COPY",FACE,{"derivedFrom":subQ1,"instanceName":"119"}),makeQuery(id+"F3.opPattern","COPY",FACE,{"derivedFrom":subQ1,"instanceName":"120"}),makeQuery(id+"F3.opPattern","COPY",FACE,{"derivedFrom":subQ1,"instanceName":"121"}),makeQuery(id+"F3.opPattern","COPY",FACE,{"derivedFrom":subQ1,"instanceName":"122"}),makeQuery(id+"F3.opPattern","COPY",FACE,{"derivedFrom":subQ1,"instanceName":"123"}),makeQuery(id+"F3.opPattern","COPY",FACE,{"derivedFrom":subQ1,"instanceName":"124"}),makeQuery(id+"F3.opPattern","COPY",FACE,{"derivedFrom":subQ1,"instanceName":"125"}),makeQuery(id+"F3.opPattern","COPY",FACE,{"derivedFrom":subQ1,"instanceName":"126"}),makeQuery(id+"F3.opPattern","COPY",FACE,{"derivedFrom":subQ1,"instanceName":"127"}),makeQuery(id+"F3.opPattern","COPY",FACE,{"derivedFrom":subQ1,"instanceName":"128"}),makeQuery(id+"F3.opPattern","COPY",FACE,{"derivedFrom":subQ1,"instanceName":"129"}),makeQuery(id+"F3.opPattern","COPY",FACE,{"derivedFrom":subQ1,"instanceName":"130"}),makeQuery(id+"F3.opPattern","COPY",FACE,{"derivedFrom":subQ1,"instanceName":"131"})]});}
            var sketch = newSketch(context, id + "F13", { "sketchPlane" : qUnion([Q0])});
            skCircle(sketch, "E37.0", {"center": v(-23.81, 0) * mm, "radius": 2.41 * mm});
            skCircle(sketch, "E37.1", {"center": v(-11.9, 20.62) * mm, "radius": 2.41 * mm});
            skCircle(sketch, "E37.2", {"center": v(11.9, 20.62) * mm, "radius": 2.41 * mm});
            skCircle(sketch, "E37.3", {"center": v(23.81, 0) * mm, "radius": 2.41 * mm});
            skCircle(sketch, "E37.4", {"center": v(11.9, -20.62) * mm, "radius": 2.41 * mm});
            skCircle(sketch, "E37.5", {"center": v(-11.9, -20.62) * mm, "radius": 2.41 * mm});
            skSolve(sketch);
        }
        {
            var Q0;
            Q0=sQuery(id+"F13.wireOp",VERTEX,"E37.4.center");
            var Q1;
            Q1=sQuery(id+"F13.wireOp",VERTEX,"E37.3.center");
            var Q2;
            Q2=sQuery(id+"F13.wireOp",VERTEX,"E37.2.center");
            var Q3;
            Q3=sQuery(id+"F13.wireOp",VERTEX,"E37.1.center");
            var Q4;
            Q4=sQuery(id+"F13.wireOp",VERTEX,"E37.0.center");
            var Q5;
            Q5=sQuery(id+"F13.wireOp",VERTEX,"E37.5.center");
            var Q6;
            Q6=makeQuery(id+"F1.opExtrude","SWEPT_BODY",BODY,{"disambiguationData":[OSD([sQuery(id+"F0.wireOp",EDGE,"E0"),sQuery(id+"F0.wireOp",EDGE,"E1"),sQuery(id+"F0.wireOp",EDGE,"E7")])]});
            hole(context, id + "F14", {"style" : HoleStyle.C_BORE, "holeDiameter" : 4.83 * mm, "cBoreDiameter" : 7.94 * mm, "cBoreDepth" : 4.83 * mm, "endStyle" : HoleEndStyle.THROUGH, "locations" : qUnion([Q0, Q1, Q2, Q3, Q4, Q5]), "scope" : qUnion([Q6])});
        }
    });
